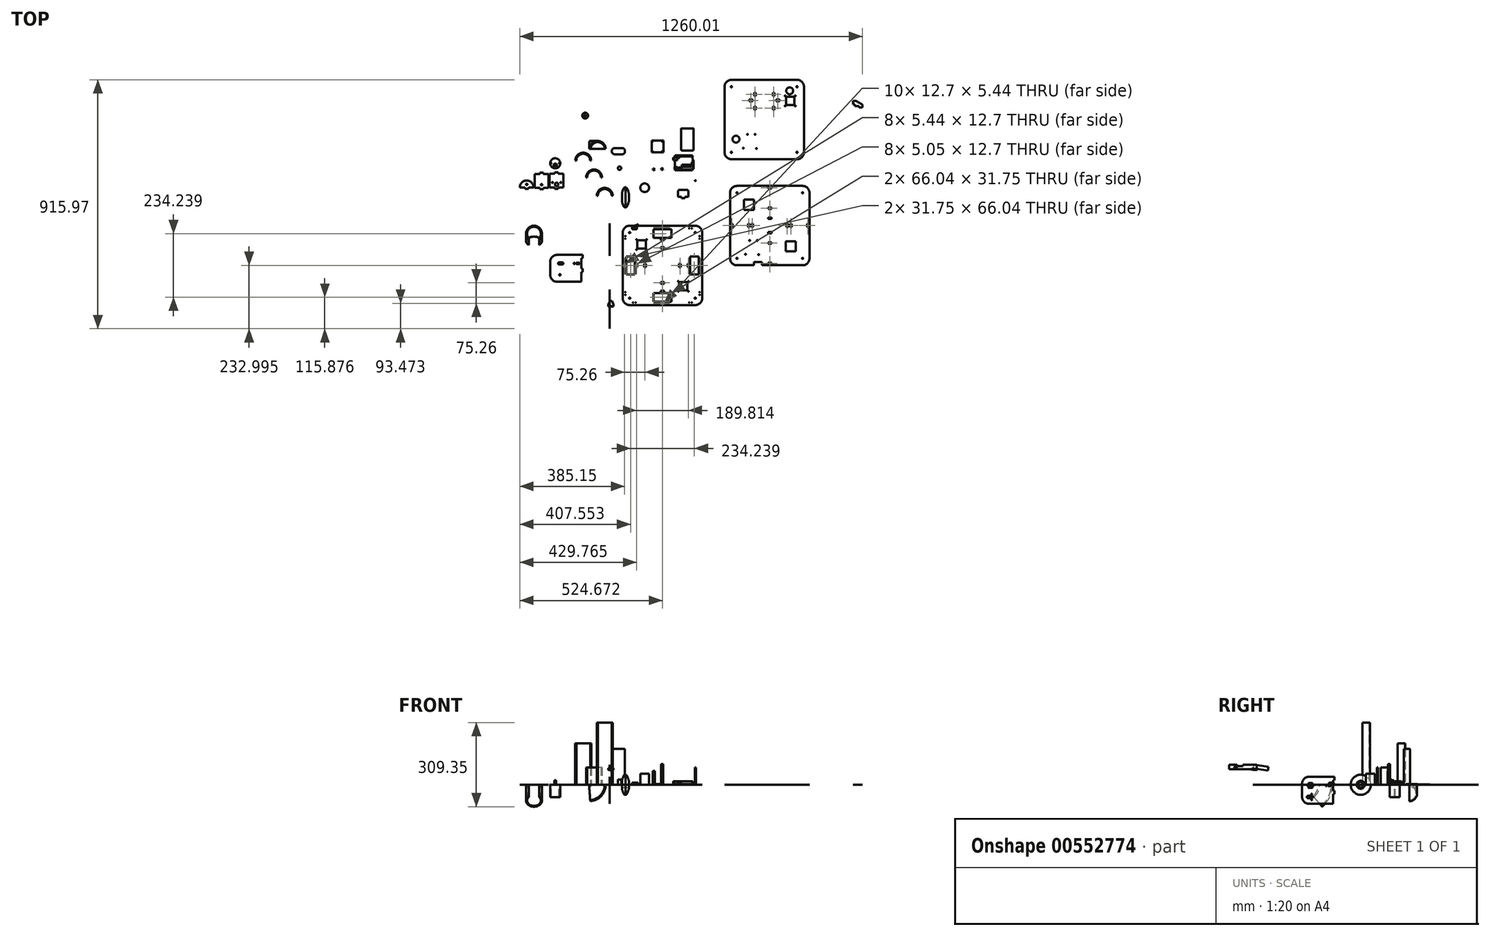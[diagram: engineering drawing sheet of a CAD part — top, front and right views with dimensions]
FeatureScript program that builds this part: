
annotation { "Feature Type Name" : "Feature", "Feature Type Description" : "" }
export const myFeature = defineFeature(function(context is Context, id is Id, definition is map)
    precondition{}
    {
        {
            assignVariable(context, id + "F0", {"name" : "T0", "anyValue" : .214});
        }
        {
            var Q0;
            Q0=qCreatedBy(makeId("Top.planeOp"),FACE);
            var sketch = newSketch(context, id + "F1", { "sketchPlane" : qUnion([Q0])});
            skCircle(sketch, "E0", {"center": v(-195, -13.55) * mm, "radius": 6.25 * mm});
            skCircle(sketch, "E1", {"center": v(-210.5, -6.55) * mm, "radius": 1.7 * mm});
            skCircle(sketch, "E2", {"center": v(-250.53, -14.94) * mm, "radius": 2.48 * mm});
            skLineSegment(sketch, "E3", {"start": v(-250.53, 35.96) * mm, "end": v(-250.53, -27.42) * mm, "construction": true});
            skLineSegment(sketch, "E4", {"start": v(-195, -13.55) * mm, "end": v(-195, 25.75) * mm, "construction": true});
            skLineSegment(sketch, "E5.bottom", {"start": v(-220.4, -25.05) * mm, "end": v(-201.34, -25.05) * mm});
            skLineSegment(sketch, "E5.top", {"start": v(-220.4, 25.75) * mm, "end": v(-201.34, 25.75) * mm});
            skLineSegment(sketch, "E5.left", {"start": v(-220.4, -25.05) * mm, "end": v(-220.4, 25.75) * mm});
            skLineSegment(sketch, "E5.right", {"start": v(-169.6, -25.05) * mm, "end": v(-169.6, 25.75) * mm});
            skLineSegment(sketch, "E6.top", {"start": v(-188.64, -30.48) * mm, "end": v(-201.34, -30.48) * mm});
            skLineSegment(sketch, "E6.left", {"start": v(-188.64, -25.05) * mm, "end": v(-188.64, -30.48) * mm});
            skLineSegment(sketch, "E6.right", {"start": v(-201.34, -25.05) * mm, "end": v(-201.34, -30.48) * mm});
            skPoint(sketch, "E6.middle", {"position": v(-195, -27.76) * mm});
            skCircle(sketch, "E7.MirrorC", {"center": v(-179.5, -6.55) * mm, "radius": 1.7 * mm});
            skLineSegment(sketch, "E8.trimOffspring", {"start": v(-188.64, -25.05) * mm, "end": v(-169.6, -25.05) * mm});
            skLineSegment(sketch, "E9.top", {"start": v(-188.64, 31.2) * mm, "end": v(-201.34, 31.2) * mm});
            skLineSegment(sketch, "E9.left", {"start": v(-188.64, 25.75) * mm, "end": v(-188.64, 31.2) * mm});
            skLineSegment(sketch, "E9.right", {"start": v(-201.34, 25.75) * mm, "end": v(-201.34, 31.2) * mm});
            skPoint(sketch, "E9.middle", {"position": v(-195, 28.47) * mm});
            skLineSegment(sketch, "E10.trimOffspring", {"start": v(-188.64, 25.75) * mm, "end": v(-169.6, 25.75) * mm});
            skLineSegment(sketch, "E11.bottom", {"start": v(-225.13, 24.36) * mm, "end": v(-244.18, 24.36) * mm});
            skLineSegment(sketch, "E11.top", {"start": v(-225.13, -26.44) * mm, "end": v(-244.18, -26.44) * mm});
            skLineSegment(sketch, "E11.left", {"start": v(-225.13, 24.36) * mm, "end": v(-225.13, -26.44) * mm});
            skLineSegment(sketch, "E11.right", {"start": v(-275.93, 24.36) * mm, "end": v(-275.93, -26.44) * mm});
            skPoint(sketch, "E11.middle", {"position": v(-250.53, -1.04) * mm});
            skLineSegment(sketch, "E12.top", {"start": v(-244.18, 29.8) * mm, "end": v(-256.88, 29.8) * mm});
            skLineSegment(sketch, "E12.left", {"start": v(-244.18, 24.36) * mm, "end": v(-244.18, 29.8) * mm});
            skLineSegment(sketch, "E12.right", {"start": v(-256.88, 24.36) * mm, "end": v(-256.88, 29.8) * mm});
            skPoint(sketch, "E12.middle", {"position": v(-250.53, 27.08) * mm});
            skLineSegment(sketch, "E13.trimOffspring", {"start": v(-256.88, 24.36) * mm, "end": v(-275.93, 24.36) * mm});
            skLineSegment(sketch, "E14.top", {"start": v(-244.18, -31.88) * mm, "end": v(-256.88, -31.88) * mm});
            skLineSegment(sketch, "E14.left", {"start": v(-244.18, -26.44) * mm, "end": v(-244.18, -31.88) * mm});
            skLineSegment(sketch, "E14.right", {"start": v(-256.88, -26.44) * mm, "end": v(-256.88, -31.88) * mm});
            skPoint(sketch, "E14.middle", {"position": v(-250.53, -29.16) * mm});
            skLineSegment(sketch, "E15.trimOffspring", {"start": v(-256.88, -26.44) * mm, "end": v(-275.93, -26.44) * mm});
            skCircle(sketch, "E16", {"center": v(-304.98, -13.55) * mm, "radius": 2.48 * mm});
            skLineSegment(sketch, "E17", {"start": v(-310.06, 36.93) * mm, "end": v(-310.06, -26.44) * mm, "construction": true});
            skLineSegment(sketch, "E18.top", {"start": v(-279.58, -25.05) * mm, "end": v(-298.63, -25.05) * mm});
            skPoint(sketch, "E18.middle", {"position": v(-304.98, 0.35) * mm});
            skLineSegment(sketch, "E19.top", {"start": v(-298.63, -30.48) * mm, "end": v(-311.33, -30.48) * mm});
            skLineSegment(sketch, "E19.left", {"start": v(-298.63, -25.05) * mm, "end": v(-298.63, -30.48) * mm});
            skLineSegment(sketch, "E19.right", {"start": v(-311.33, -25.05) * mm, "end": v(-311.33, -30.48) * mm});
            skPoint(sketch, "E19.middle", {"position": v(-304.98, -27.76) * mm});
            skLineSegment(sketch, "E20.trimOffspring", {"start": v(-311.33, -25.05) * mm, "end": v(-330.38, -25.05) * mm});
            skArc(sketch, "E21", {"start": v(-279.58, -25.05) * mm, "mid": v(-304.98, 0.35) * mm, "end": v(-330.38, -25.05) * mm});
            skSolve(sketch);
        }
        {
            var Q0;
            Q0=qCreatedBy(makeId("Top.planeOp"),FACE);
            var sketch = newSketch(context, id + "F2", { "sketchPlane" : qUnion([Q0])});
            skCircle(sketch, "E22", {"center": v(-200.16, 64.01) * mm, "radius": 18.5 * mm});
            skLineSegment(sketch, "E23", {"start": v(-200.16, 64.01) * mm, "end": v(-200.16, 82.51) * mm, "construction": true});
            skLineSegment(sketch, "E24", {"start": v(-200.16, 64.01) * mm, "end": v(-218.66, 64.01) * mm, "construction": true});
            skCircle(sketch, "E25", {"center": v(-215.66, 64.01) * mm, "radius": 1.7 * mm});
            skLineSegment(sketch, "E26", {"start": v(-200.16, 64.01) * mm, "end": v(-200.16, 45.51) * mm, "construction": true});
            skCircle(sketch, "E27", {"center": v(-200.16, 57.01) * mm, "radius": 3 * mm});
            skCircle(sketch, "E28.MirrorC", {"center": v(-184.66, 64.01) * mm, "radius": 1.7 * mm});
            skCircle(sketch, "E29", {"center": v(-200.16, 57.01) * mm, "radius": 6 * mm});
            skSolve(sketch);
        }
        {
            var Q0;
            Q0=makeQuery(id+"F2.imprint","IMPRINT",FACE,{"disambiguationData":[TD([[makeQuery(id+"F2.imprint","IMPRINT",EDGE,{"derivedFrom":sQuery(id+"F2.wireOp",EDGE,"VeMokPUN-uezl-VlB1-s7x8-Obfx0nJFnMSX")}),1.0]])]});
            var Q1;
            Q1=makeQuery(id+"F2.imprint","IMPRINT",FACE,{"disambiguationData":[TD([[makeQuery(id+"F2.imprint","IMPRINT",EDGE,{"derivedFrom":sQuery(id+"F2.wireOp",EDGE,"E22")}),1.0]])]});
            var Q2;
            Q2=makeQuery(id+"F2.imprint","IMPRINT",FACE,{"disambiguationData":[TD([[makeQuery(id+"F2.imprint","IMPRINT",EDGE,{"derivedFrom":sQuery(id+"F2.wireOp",EDGE,"E27")}),1.0]])]});
            var Q3;
            Q3=makeQuery(id+"F2.imprint","IMPRINT",FACE,{"disambiguationData":[TD([[makeQuery(id+"F2.imprint","IMPRINT",EDGE,{"derivedFrom":sQuery(id+"F2.wireOp",EDGE,"E27")}),-1.0]])]});
            extrude(context, id + "F3", {"entities" : qUnion([Q0, Q1, Q2, Q3]), "oppositeDirection" : true, "depth" : 45.4 * mm, "offsetDistance" : 25.4 * mm});
        }
        {
            var Q0;
            Q0=makeQuery(id+"F3.opExtrude","CAP_FACE",FACE,{"disambiguationData":[OSD([sQuery(id+"F2.wireOp",EDGE,"E22"),sQuery(id+"F2.wireOp",EDGE,"E25"),sQuery(id+"F2.wireOp",EDGE,"E28.MirrorC")])],"isStart":true});
            var sketch = newSketch(context, id + "F4", { "sketchPlane" : qUnion([Q0])});
            skLineSegment(sketch, "E30", {"start": v(-215.66, 64.01) * mm, "end": v(-184.66, 64.01) * mm, "construction": true});
            skLineSegment(sketch, "E31", {"start": v(-200.16, 64.01) * mm, "end": v(-200.16, 45.51) * mm, "construction": true});
            skCircle(sketch, "E32", {"center": v(-200.16, 57.01) * mm, "radius": 6 * mm});
            skSolve(sketch);
        }
        {
            var Q0;
            Q0=makeQuery(id+"F4.imprint","IMPRINT",FACE,{"disambiguationData":[TD([[makeQuery(id+"F4.imprint","IMPRINT",EDGE,{"derivedFrom":sQuery(id+"F4.wireOp",EDGE,"E32")}),1.0]])]});
            extrude(context, id + "F5", {"entities" : qUnion([Q0]), "operationType" : NewBodyOperationType.ADD, "depth" : 4 * mm, "offsetDistance" : 25.4 * mm});
        }
        {
            var Q0;
            Q0=makeQuery(id+"F5.opExtrude","CAP_FACE",FACE,{"disambiguationData":[OSD([sQuery(id+"F4.wireOp",EDGE,"E32")])],"isStart":false});
            var sketch = newSketch(context, id + "F6", { "sketchPlane" : qUnion([Q0])});
            skCircle(sketch, "E33", {"center": v(-200.16, 57.01) * mm, "radius": 3 * mm});
            skSolve(sketch);
        }
        {
            var Q0;
            Q0=makeQuery(id+"F6.imprint","IMPRINT",FACE,{"disambiguationData":[TD([[makeQuery(id+"F6.imprint","IMPRINT",EDGE,{"derivedFrom":sQuery(id+"F6.wireOp",EDGE,"E33")}),1.0]])]});
            extrude(context, id + "F7", {"entities" : qUnion([Q0]), "operationType" : NewBodyOperationType.ADD, "depth" : 13 * mm, "offsetDistance" : 25.4 * mm});
        }
        {
            var Q0;
            Q0=qCreatedBy(makeId("Top.planeOp"),FACE);
            var sketch = newSketch(context, id + "F8", { "sketchPlane" : qUnion([Q0])});
            skLineSegment(sketch, "E34.bottom", {"start": v(154.77, 147.35) * mm, "end": v(197.77, 147.35) * mm});
            skLineSegment(sketch, "E34.top", {"start": v(154.77, 104.35) * mm, "end": v(197.77, 104.35) * mm});
            skLineSegment(sketch, "E34.left", {"start": v(154.77, 147.35) * mm, "end": v(154.77, 104.35) * mm});
            skLineSegment(sketch, "E34.right", {"start": v(197.77, 147.35) * mm, "end": v(197.77, 104.35) * mm});
            skCircle(sketch, "E35", {"center": v(157.22, 144.54) * mm, "radius": 1.74 * mm});
            skCircle(sketch, "E36.0.1.0", {"center": v(157.22, 107.54) * mm, "radius": 1.74 * mm});
            skCircle(sketch, "E36.1.0.0", {"center": v(194.22, 144.54) * mm, "radius": 1.74 * mm});
            skCircle(sketch, "E36.1.1.0", {"center": v(194.22, 107.54) * mm, "radius": 1.74 * mm});
            skLineSegment(sketch, "E36.direction1", {"start": v(157.22, 144.54) * mm, "end": v(194.22, 144.54) * mm, "construction": true});
            skLineSegment(sketch, "E36.direction2", {"start": v(157.22, 144.54) * mm, "end": v(157.22, 107.54) * mm, "construction": true});
            skSolve(sketch);
        }
        {
            var Q0;
            Q0 = qSketchRegion(id + "F8", true);
            extrude(context, id + "F9", {"entities" : qUnion([Q0]), "depth" : 2.03 * mm, "offsetDistance" : 25.4 * mm});
        }
        {
            var Q0;
            Q0=qCreatedBy(makeId("Top.planeOp"),FACE);
            var sketch = newSketch(context, id + "F10", { "sketchPlane" : qUnion([Q0])});
            skLineSegment(sketch, "E37.bottom", {"start": v(18.32, 97.14) * mm, "end": v(46.26, 97.14) * mm});
            skLineSegment(sketch, "E37.top", {"start": v(18.32, 120) * mm, "end": v(46.26, 120) * mm});
            skLineSegment(sketch, "E37.left", {"start": v(8.16, 107.3) * mm, "end": v(8.16, 109.84) * mm});
            skLineSegment(sketch, "E37.right", {"start": v(56.42, 107.3) * mm, "end": v(56.42, 109.84) * mm});
            skPoint(sketch, "E38.visualSharp", {"position": v(8.16, 120) * mm});
            skArc(sketch, "E38.filletArc", {"start": v(18.32, 120) * mm, "mid": v(11.13, 117.02) * mm, "end": v(8.16, 109.84) * mm});
            skPoint(sketch, "E39.visualSharp", {"position": v(8.16, 97.14) * mm});
            skArc(sketch, "E39.filletArc", {"start": v(8.16, 107.3) * mm, "mid": v(11.13, 100.12) * mm, "end": v(18.32, 97.14) * mm});
            skPoint(sketch, "E40.visualSharp", {"position": v(56.42, 97.14) * mm});
            skArc(sketch, "E40.filletArc", {"start": v(46.26, 97.14) * mm, "mid": v(53.44, 100.12) * mm, "end": v(56.42, 107.3) * mm});
            skPoint(sketch, "E41.visualSharp", {"position": v(56.42, 120) * mm});
            skArc(sketch, "E41.filletArc", {"start": v(56.42, 109.84) * mm, "mid": v(53.44, 117.02) * mm, "end": v(46.26, 120) * mm});
            skSolve(sketch);
        }
        {
            var Q0;
            Q0 = qSketchRegion(id + "F10", true);
            extrude(context, id + "F11", {"entities" : qUnion([Q0]), "depth" : 132.08 * mm, "offsetDistance" : 25.4 * mm});
        }
        {
            var Q0;
            Q0=qCreatedBy(makeId("Top.planeOp"),FACE);
            var sketch = newSketch(context, id + "F12", { "sketchPlane" : qUnion([Q0])});
            skLineSegment(sketch, "E42.bottom", {"start": v(240.3, 92.55) * mm, "end": v(305.07, 92.55) * mm});
            skLineSegment(sketch, "E42.top", {"start": v(240.3, 38.58) * mm, "end": v(305.07, 38.58) * mm});
            skLineSegment(sketch, "E42.left", {"start": v(240.3, 92.55) * mm, "end": v(240.3, 38.58) * mm});
            skLineSegment(sketch, "E42.right", {"start": v(305.07, 92.55) * mm, "end": v(305.07, 78.55) * mm});
            skLineSegment(sketch, "E43", {"start": v(305.07, 78.55) * mm, "end": v(308.97, 75.22) * mm});
            skLineSegment(sketch, "E44", {"start": v(308.97, 75.22) * mm, "end": v(308.97, 43.61) * mm});
            skLineSegment(sketch, "E45", {"start": v(308.97, 43.61) * mm, "end": v(305.07, 40.9) * mm});
            skLineSegment(sketch, "E46.trimOffspring", {"start": v(305.07, 40.9) * mm, "end": v(305.07, 38.58) * mm});
            skCircle(sketch, "E47", {"center": v(254.27, 41.12) * mm, "radius": 1.59 * mm});
            skCircle(sketch, "E48", {"center": v(306.34, 46.2) * mm, "radius": 1.59 * mm});
            skCircle(sketch, "E49", {"center": v(306.34, 74.14) * mm, "radius": 1.59 * mm});
            skCircle(sketch, "E50", {"center": v(255.54, 89.38) * mm, "radius": 1.59 * mm});
            skSolve(sketch);
        }
        {
            var Q0;
            Q0 = qSketchRegion(id + "F12", true);
            extrude(context, id + "F13", {"entities" : qUnion([Q0]), "depth" : 3.17 * mm, "offsetDistance" : 25.4 * mm});
        }
        {
            var Q0;
            Q0=makeQuery(id+"F13.opExtrude","CAP_FACE",FACE,{"disambiguationData":[OSD([sQuery(id+"F12.wireOp",EDGE,"E42.bottom"),sQuery(id+"F12.wireOp",EDGE,"E42.top"),sQuery(id+"F12.wireOp",EDGE,"E42.left"),sQuery(id+"F12.wireOp",EDGE,"E42.right"),sQuery(id+"F12.wireOp",EDGE,"E43"),sQuery(id+"F12.wireOp",EDGE,"E44"),sQuery(id+"F12.wireOp",EDGE,"E45"),sQuery(id+"F12.wireOp",EDGE,"E46.trimOffspring")])],"isStart":false});
            var sketch = newSketch(context, id + "F14", { "sketchPlane" : qUnion([Q0])});
            skLineSegment(sketch, "E51.bottom", {"start": v(253.63, 91.4) * mm, "end": v(305.07, 91.4) * mm});
            skLineSegment(sketch, "E51.top", {"start": v(253.63, 89.59) * mm, "end": v(305.07, 89.59) * mm});
            skLineSegment(sketch, "E51.left", {"start": v(253.63, 91.4) * mm, "end": v(253.63, 89.59) * mm});
            skLineSegment(sketch, "E51.right", {"start": v(305.07, 91.4) * mm, "end": v(305.07, 89.59) * mm});
            skLineSegment(sketch, "E52.bottom", {"start": v(260.74, 39.85) * mm, "end": v(303.83, 39.85) * mm});
            skLineSegment(sketch, "E52.top", {"start": v(260.74, 41.36) * mm, "end": v(303.83, 41.36) * mm});
            skLineSegment(sketch, "E52.left", {"start": v(260.74, 39.85) * mm, "end": v(260.74, 41.36) * mm});
            skLineSegment(sketch, "E52.right", {"start": v(303.83, 39.85) * mm, "end": v(303.83, 41.36) * mm});
            skLineSegment(sketch, "E53.bottom", {"start": v(264.97, 58.14) * mm, "end": v(300.65, 58.14) * mm});
            skLineSegment(sketch, "E53.top", {"start": v(264.97, 51.03) * mm, "end": v(300.65, 51.03) * mm});
            skLineSegment(sketch, "E53.left", {"start": v(264.97, 58.14) * mm, "end": v(264.97, 51.03) * mm});
            skLineSegment(sketch, "E53.right", {"start": v(300.65, 58.14) * mm, "end": v(300.65, 51.03) * mm});
            skCircle(sketch, "E54", {"center": v(255.9, 46.65) * mm, "radius": 2.27 * mm});
            skCircle(sketch, "E55", {"center": v(261.2, 46.65) * mm, "radius": 2.46 * mm});
            skLineSegment(sketch, "E56.bottom", {"start": v(238.52, 49.52) * mm, "end": v(250.61, 49.52) * mm});
            skLineSegment(sketch, "E56.top", {"start": v(238.52, 43.17) * mm, "end": v(250.61, 43.17) * mm});
            skLineSegment(sketch, "E56.left", {"start": v(238.52, 49.52) * mm, "end": v(238.52, 43.17) * mm});
            skLineSegment(sketch, "E56.right", {"start": v(250.61, 49.52) * mm, "end": v(250.61, 43.17) * mm});
            skLineSegment(sketch, "E57.bottom", {"start": v(233.38, 85.35) * mm, "end": v(248.34, 85.35) * mm});
            skLineSegment(sketch, "E57.top", {"start": v(233.38, 75.22) * mm, "end": v(248.34, 75.22) * mm});
            skLineSegment(sketch, "E57.left", {"start": v(233.38, 85.35) * mm, "end": v(233.38, 75.22) * mm});
            skLineSegment(sketch, "E57.right", {"start": v(248.34, 85.35) * mm, "end": v(248.34, 75.22) * mm});
            skLineSegment(sketch, "E58.bottom", {"start": v(302.77, 68.72) * mm, "end": v(305.8, 68.72) * mm});
            skLineSegment(sketch, "E58.top", {"start": v(302.77, 63.28) * mm, "end": v(305.8, 63.28) * mm});
            skLineSegment(sketch, "E58.left", {"start": v(302.77, 68.72) * mm, "end": v(302.77, 63.28) * mm});
            skLineSegment(sketch, "E58.right", {"start": v(305.8, 68.72) * mm, "end": v(305.8, 63.28) * mm});
            skLineSegment(sketch, "E59.bottom", {"start": v(250.91, 87.62) * mm, "end": v(257.41, 87.62) * mm});
            skLineSegment(sketch, "E59.top", {"start": v(250.91, 84.45) * mm, "end": v(257.41, 84.45) * mm});
            skLineSegment(sketch, "E59.left", {"start": v(250.91, 87.62) * mm, "end": v(250.91, 84.45) * mm});
            skLineSegment(sketch, "E59.right", {"start": v(257.41, 87.62) * mm, "end": v(257.41, 84.45) * mm});
            skSolve(sketch);
        }
        {
            var Q0;
            Q0 = qSketchRegion(id + "F14", true);
            extrude(context, id + "F15", {"entities" : qUnion([Q0]), "operationType" : NewBodyOperationType.ADD, "depth" : 9.52 * mm, "offsetDistance" : 25.4 * mm});
        }
        {
            var Q0;
            Q0 = qSketchRegion(id + "F1", true);
            extrude(context, id + "F16", {"entities" : qUnion([Q0]), "depth" : (getVariable(context, 'T0')) * mm, "offsetDistance" : 25.4 * mm});
        }
        {
            var Q0;
            Q0=qCreatedBy(makeId("Top.planeOp"),FACE);
            var sketch = newSketch(context, id + "F17", { "sketchPlane" : qUnion([Q0])});
            skLineSegment(sketch, "E60.bottom", {"start": v(314.94, -165.87) * mm, "end": v(73.64, -165.87) * mm});
            skLineSegment(sketch, "E60.top", {"start": v(314.94, -457.97) * mm, "end": v(73.64, -457.97) * mm});
            skLineSegment(sketch, "E60.left", {"start": v(340.34, -191.27) * mm, "end": v(340.34, -432.57) * mm});
            skLineSegment(sketch, "E60.right", {"start": v(48.24, -191.27) * mm, "end": v(48.24, -432.57) * mm});
            skPoint(sketch, "E60.middle", {"position": v(194.3, -311.92) * mm});
            skPoint(sketch, "E61.visualSharp", {"position": v(48.24, -165.87) * mm});
            skArc(sketch, "E61.filletArc", {"start": v(73.64, -165.87) * mm, "mid": v(55.68, -173.31) * mm, "end": v(48.24, -191.27) * mm});
            skPoint(sketch, "E62.visualSharp", {"position": v(340.34, -165.87) * mm});
            skArc(sketch, "E62.filletArc", {"start": v(340.34, -191.27) * mm, "mid": v(332.9, -173.31) * mm, "end": v(314.94, -165.87) * mm});
            skPoint(sketch, "E63.visualSharp", {"position": v(340.34, -457.97) * mm});
            skArc(sketch, "E63.filletArc", {"start": v(314.94, -457.97) * mm, "mid": v(332.9, -450.54) * mm, "end": v(340.34, -432.57) * mm});
            skPoint(sketch, "E64.visualSharp", {"position": v(48.24, -457.97) * mm});
            skArc(sketch, "E64.filletArc", {"start": v(48.24, -432.57) * mm, "mid": v(55.68, -450.54) * mm, "end": v(73.64, -457.97) * mm});
            skLineSegment(sketch, "E65", {"start": v(194.3, -165.87) * mm, "end": v(194.3, -311.92) * mm, "construction": true});
            skLineSegment(sketch, "E66.bottom", {"start": v(200.64, -169.68) * mm, "end": v(187.94, -169.68) * mm});
            skLineSegment(sketch, "E66.top", {"start": v(200.64, -175.12) * mm, "end": v(187.94, -175.12) * mm});
            skLineSegment(sketch, "E66.left", {"start": v(200.64, -169.68) * mm, "end": v(200.64, -175.12) * mm});
            skLineSegment(sketch, "E66.right", {"start": v(187.94, -169.68) * mm, "end": v(187.94, -175.12) * mm});
            skPoint(sketch, "E66.middle", {"position": v(194.3, -172.4) * mm});
            skLineSegment(sketch, "E67.bottom", {"start": v(227.31, -178.93) * mm, "end": v(161.27, -178.93) * mm});
            skLineSegment(sketch, "E67.top", {"start": v(227.31, -210.68) * mm, "end": v(161.27, -210.68) * mm});
            skLineSegment(sketch, "E67.left", {"start": v(227.31, -178.93) * mm, "end": v(227.31, -210.68) * mm});
            skLineSegment(sketch, "E67.right", {"start": v(161.27, -178.93) * mm, "end": v(161.27, -210.68) * mm});
            skPoint(sketch, "E67.middle", {"position": v(194.3, -194.8) * mm});
            skPoint(sketch, "E68.middle", {"position": v(194.3, -217.02) * mm});
            skLineSegment(sketch, "E69.bottom", {"start": v(200.64, -214.5) * mm, "end": v(187.94, -214.5) * mm});
            skLineSegment(sketch, "E69.top", {"start": v(200.64, -219.55) * mm, "end": v(187.94, -219.55) * mm});
            skLineSegment(sketch, "E69.left", {"start": v(200.64, -214.5) * mm, "end": v(200.64, -219.55) * mm});
            skLineSegment(sketch, "E69.right", {"start": v(187.94, -214.5) * mm, "end": v(187.94, -219.55) * mm});
            skLineSegment(sketch, "E70.bottom", {"start": v(200.64, -244.95) * mm, "end": v(187.94, -244.95) * mm});
            skLineSegment(sketch, "E70.top", {"start": v(200.64, -250.38) * mm, "end": v(187.94, -250.38) * mm});
            skLineSegment(sketch, "E70.left", {"start": v(200.64, -244.95) * mm, "end": v(200.64, -250.38) * mm});
            skLineSegment(sketch, "E70.right", {"start": v(187.94, -244.95) * mm, "end": v(187.94, -250.38) * mm});
            skPoint(sketch, "E70.middle", {"position": v(194.3, -247.66) * mm});
            skCircle(sketch, "E71", {"center": v(73.64, -191.27) * mm, "radius": 2.13 * mm});
            skCircle(sketch, "E72.1.0", {"center": v(314.94, -191.27) * mm, "radius": 2.13 * mm});
            skLineSegment(sketch, "E72.1.1", {"start": v(327.29, -278.9) * mm, "end": v(295.54, -278.9) * mm});
            skLineSegment(sketch, "E72.1.2", {"start": v(327.29, -344.94) * mm, "end": v(327.29, -278.9) * mm});
            skLineSegment(sketch, "E72.1.3", {"start": v(295.54, -344.94) * mm, "end": v(295.54, -278.9) * mm});
            skLineSegment(sketch, "E72.1.4", {"start": v(327.29, -344.94) * mm, "end": v(295.54, -344.94) * mm});
            skLineSegment(sketch, "E72.1.5", {"start": v(331.1, -318.27) * mm, "end": v(331.1, -305.57) * mm});
            skLineSegment(sketch, "E72.1.6", {"start": v(336.53, -305.57) * mm, "end": v(331.1, -305.57) * mm});
            skLineSegment(sketch, "E72.1.7", {"start": v(336.53, -318.27) * mm, "end": v(336.53, -305.57) * mm});
            skLineSegment(sketch, "E72.1.8", {"start": v(336.53, -318.27) * mm, "end": v(331.1, -318.27) * mm});
            skLineSegment(sketch, "E72.1.9", {"start": v(291.73, -318.27) * mm, "end": v(291.73, -305.57) * mm});
            skLineSegment(sketch, "E72.1.10", {"start": v(291.73, -305.57) * mm, "end": v(286.67, -305.57) * mm});
            skLineSegment(sketch, "E72.1.11", {"start": v(286.67, -318.27) * mm, "end": v(286.67, -305.57) * mm});
            skLineSegment(sketch, "E72.1.12", {"start": v(291.73, -318.27) * mm, "end": v(286.67, -318.27) * mm});
            skLineSegment(sketch, "E72.1.13", {"start": v(261.27, -318.27) * mm, "end": v(261.27, -305.57) * mm});
            skLineSegment(sketch, "E72.1.14", {"start": v(261.27, -318.27) * mm, "end": v(255.84, -318.27) * mm});
            skLineSegment(sketch, "E72.1.15", {"start": v(255.84, -318.27) * mm, "end": v(255.84, -305.57) * mm});
            skLineSegment(sketch, "E72.1.16", {"start": v(261.27, -305.57) * mm, "end": v(255.84, -305.57) * mm});
            skCircle(sketch, "E72.2.0", {"center": v(314.94, -432.57) * mm, "radius": 2.13 * mm});
            skLineSegment(sketch, "E72.2.1", {"start": v(227.31, -444.92) * mm, "end": v(227.31, -413.17) * mm});
            skLineSegment(sketch, "E72.2.2", {"start": v(161.27, -444.92) * mm, "end": v(227.31, -444.92) * mm});
            skLineSegment(sketch, "E72.2.3", {"start": v(161.27, -413.17) * mm, "end": v(227.31, -413.17) * mm});
            skLineSegment(sketch, "E72.2.4", {"start": v(161.27, -444.92) * mm, "end": v(161.27, -413.17) * mm});
            skLineSegment(sketch, "E72.2.5", {"start": v(187.94, -448.73) * mm, "end": v(200.64, -448.73) * mm});
            skLineSegment(sketch, "E72.2.6", {"start": v(200.64, -454.16) * mm, "end": v(200.64, -448.73) * mm});
            skLineSegment(sketch, "E72.2.7", {"start": v(187.94, -454.16) * mm, "end": v(200.64, -454.16) * mm});
            skLineSegment(sketch, "E72.2.8", {"start": v(187.94, -454.16) * mm, "end": v(187.94, -448.73) * mm});
            skLineSegment(sketch, "E72.2.9", {"start": v(187.94, -409.36) * mm, "end": v(200.64, -409.36) * mm});
            skLineSegment(sketch, "E72.2.10", {"start": v(200.64, -409.36) * mm, "end": v(200.64, -404.3) * mm});
            skLineSegment(sketch, "E72.2.11", {"start": v(187.94, -404.3) * mm, "end": v(200.64, -404.3) * mm});
            skLineSegment(sketch, "E72.2.12", {"start": v(187.94, -409.36) * mm, "end": v(187.94, -404.3) * mm});
            skLineSegment(sketch, "E72.2.13", {"start": v(187.94, -378.9) * mm, "end": v(200.64, -378.9) * mm});
            skLineSegment(sketch, "E72.2.14", {"start": v(187.94, -378.9) * mm, "end": v(187.94, -373.47) * mm});
            skLineSegment(sketch, "E72.2.15", {"start": v(187.94, -373.47) * mm, "end": v(200.64, -373.47) * mm});
            skLineSegment(sketch, "E72.2.16", {"start": v(200.64, -378.9) * mm, "end": v(200.64, -373.47) * mm});
            skCircle(sketch, "E72.3.0", {"center": v(73.64, -432.57) * mm, "radius": 2.13 * mm});
            skLineSegment(sketch, "E72.3.1", {"start": v(61.3, -344.94) * mm, "end": v(93.05, -344.94) * mm});
            skLineSegment(sketch, "E72.3.2", {"start": v(61.3, -278.9) * mm, "end": v(61.3, -344.94) * mm});
            skLineSegment(sketch, "E72.3.3", {"start": v(93.05, -278.9) * mm, "end": v(93.05, -344.94) * mm});
            skLineSegment(sketch, "E72.3.4", {"start": v(61.3, -278.9) * mm, "end": v(93.05, -278.9) * mm});
            skLineSegment(sketch, "E72.3.5", {"start": v(57.49, -305.57) * mm, "end": v(57.49, -318.27) * mm});
            skLineSegment(sketch, "E72.3.6", {"start": v(52.05, -318.27) * mm, "end": v(57.49, -318.27) * mm});
            skLineSegment(sketch, "E72.3.7", {"start": v(52.05, -305.57) * mm, "end": v(52.05, -318.27) * mm});
            skLineSegment(sketch, "E72.3.8", {"start": v(52.05, -305.57) * mm, "end": v(57.49, -305.57) * mm});
            skLineSegment(sketch, "E72.3.9", {"start": v(96.86, -305.57) * mm, "end": v(96.86, -318.27) * mm});
            skLineSegment(sketch, "E72.3.10", {"start": v(96.86, -318.27) * mm, "end": v(101.91, -318.27) * mm});
            skLineSegment(sketch, "E72.3.11", {"start": v(101.91, -305.57) * mm, "end": v(101.91, -318.27) * mm});
            skLineSegment(sketch, "E72.3.12", {"start": v(96.86, -305.57) * mm, "end": v(101.91, -305.57) * mm});
            skLineSegment(sketch, "E72.3.13", {"start": v(127.31, -305.57) * mm, "end": v(127.31, -318.27) * mm});
            skLineSegment(sketch, "E72.3.14", {"start": v(127.31, -305.57) * mm, "end": v(132.75, -305.57) * mm});
            skLineSegment(sketch, "E72.3.15", {"start": v(132.75, -305.57) * mm, "end": v(132.75, -318.27) * mm});
            skLineSegment(sketch, "E72.3.16", {"start": v(127.31, -318.27) * mm, "end": v(132.75, -318.27) * mm});
            skLineSegment(sketch, "E72.anchor1", {"start": v(194.3, -311.92) * mm, "end": v(73.64, -191.27) * mm, "construction": true});
            skLineSegment(sketch, "E72.anchor2", {"start": v(194.3, -311.92) * mm, "end": v(73.64, -432.57) * mm, "construction": true});
            skCircle(sketch, "E73", {"center": v(99.04, -216.67) * mm, "radius": 1.46 * mm});
            skCircle(sketch, "E74.0.1.0", {"center": v(99.04, -253.67) * mm, "radius": 1.46 * mm});
            skCircle(sketch, "E74.1.0.0", {"center": v(136.04, -216.67) * mm, "radius": 1.46 * mm});
            skCircle(sketch, "E74.1.1.0", {"center": v(136.04, -253.67) * mm, "radius": 1.46 * mm});
            skLineSegment(sketch, "E74.direction1", {"start": v(94.2, -207.7) * mm, "end": v(130.01, -207.7) * mm, "construction": true});
            skLineSegment(sketch, "E74.direction2", {"start": v(94.2, -207.7) * mm, "end": v(94.2, -243.5) * mm, "construction": true});
            skCircle(sketch, "E75.1.0", {"center": v(252.54, -407.17) * mm, "radius": 1.46 * mm});
            skCircle(sketch, "E75.1.1", {"center": v(289.54, -407.17) * mm, "radius": 1.46 * mm});
            skCircle(sketch, "E75.1.2", {"center": v(289.54, -370.17) * mm, "radius": 1.46 * mm});
            skCircle(sketch, "E75.1.3", {"center": v(252.54, -370.17) * mm, "radius": 1.46 * mm});
            skLineSegment(sketch, "E75.anchor1", {"start": v(194.3, -311.92) * mm, "end": v(136.04, -216.67) * mm, "construction": true});
            skLineSegment(sketch, "E75.anchor2", {"start": v(194.3, -311.92) * mm, "end": v(252.54, -407.17) * mm, "construction": true});
            skCircle(sketch, "E76", {"center": v(86.34, -175.4) * mm, "radius": 1.02 * mm});
            skCircle(sketch, "E77", {"center": v(95.87, -175.4) * mm, "radius": 1.02 * mm});
            skCircle(sketch, "E78.MirrorC", {"center": v(302.24, -175.4) * mm, "radius": 1.02 * mm});
            skCircle(sketch, "E79.MirrorC", {"center": v(292.72, -175.4) * mm, "radius": 1.02 * mm});
            skCircle(sketch, "E80.1.0", {"center": v(330.82, -203.97) * mm, "radius": 1.02 * mm});
            skCircle(sketch, "E80.1.1", {"center": v(330.82, -213.5) * mm, "radius": 1.02 * mm});
            skCircle(sketch, "E80.1.2", {"center": v(330.82, -410.35) * mm, "radius": 1.02 * mm});
            skCircle(sketch, "E80.1.3", {"center": v(330.82, -419.87) * mm, "radius": 1.02 * mm});
            skCircle(sketch, "E80.2.0", {"center": v(302.24, -448.45) * mm, "radius": 1.02 * mm});
            skCircle(sketch, "E80.2.1", {"center": v(292.72, -448.45) * mm, "radius": 1.02 * mm});
            skCircle(sketch, "E80.2.2", {"center": v(95.87, -448.45) * mm, "radius": 1.02 * mm});
            skCircle(sketch, "E80.2.3", {"center": v(86.34, -448.45) * mm, "radius": 1.02 * mm});
            skCircle(sketch, "E80.3.0", {"center": v(57.77, -419.87) * mm, "radius": 1.02 * mm});
            skCircle(sketch, "E80.3.1", {"center": v(57.77, -410.35) * mm, "radius": 1.02 * mm});
            skCircle(sketch, "E80.3.2", {"center": v(57.77, -213.5) * mm, "radius": 1.02 * mm});
            skCircle(sketch, "E80.3.3", {"center": v(57.77, -203.97) * mm, "radius": 1.02 * mm});
            skLineSegment(sketch, "E80.anchor1", {"start": v(194.3, -311.92) * mm, "end": v(86.34, -175.4) * mm, "construction": true});
            skLineSegment(sketch, "E80.anchor2", {"start": v(194.3, -311.92) * mm, "end": v(57.77, -419.87) * mm, "construction": true});
            skLineSegment(sketch, "E81.bottom", {"start": v(102.22, -219.85) * mm, "end": v(132.87, -219.85) * mm});
            skLineSegment(sketch, "E81.top", {"start": v(102.22, -250.5) * mm, "end": v(132.87, -250.5) * mm});
            skLineSegment(sketch, "E81.left", {"start": v(102.22, -219.85) * mm, "end": v(102.22, -250.5) * mm});
            skLineSegment(sketch, "E81.right", {"start": v(132.87, -219.85) * mm, "end": v(132.87, -250.5) * mm});
            skLineSegment(sketch, "E82.1.0", {"start": v(43.83, 115.88) * mm, "end": v(13.18, 115.88) * mm});
            skPoint(sketch, "E82.center", {"position": v(146.05, -134.62) * mm});
            skLineSegment(sketch, "E83.1.0", {"start": v(255.72, -404) * mm, "end": v(255.72, -373.35) * mm});
            skLineSegment(sketch, "E83.1.1", {"start": v(286.37, -404) * mm, "end": v(255.72, -404) * mm});
            skLineSegment(sketch, "E83.1.2", {"start": v(286.37, -404) * mm, "end": v(286.37, -373.35) * mm});
            skLineSegment(sketch, "E83.1.3", {"start": v(286.37, -373.35) * mm, "end": v(255.72, -373.35) * mm});
            skLineSegment(sketch, "E83.anchor1", {"start": v(194.3, -311.92) * mm, "end": v(132.87, -250.5) * mm, "construction": true});
            skLineSegment(sketch, "E83.anchor2", {"start": v(194.3, -311.92) * mm, "end": v(255.72, -373.35) * mm, "construction": true});
            skSolve(sketch);
        }
        {
            var Q0;
            Q0 = qSketchRegion(id + "F17", true);
            extrude(context, id + "F18", {"entities" : qUnion([Q0]), "depth" : (getVariable(context, 'T0')) * mm, "offsetDistance" : 25.4 * mm});
        }
        {
            var Q0;
            Q0=qCreatedBy(makeId("Top.planeOp"),FACE);
            var sketch = newSketch(context, id + "F19", { "sketchPlane" : qUnion([Q0])});
            skCircle(sketch, "E84.cCircle", {"center": v(162.42, 41.36) * mm, "radius": 3.97 * mm, "construction": true});
            skLineSegment(sketch, "E84.0", {"start": v(164.37, 44.82) * mm, "end": v(166.39, 41.4) * mm});
            skLineSegment(sketch, "E84.1", {"start": v(166.39, 41.4) * mm, "end": v(164.44, 37.94) * mm});
            skLineSegment(sketch, "E84.2", {"start": v(164.44, 37.94) * mm, "end": v(160.47, 37.9) * mm});
            skLineSegment(sketch, "E84.3", {"start": v(160.47, 37.9) * mm, "end": v(158.45, 41.32) * mm});
            skLineSegment(sketch, "E84.4", {"start": v(158.45, 41.32) * mm, "end": v(160.4, 44.78) * mm});
            skLineSegment(sketch, "E84.5", {"start": v(160.4, 44.78) * mm, "end": v(164.37, 44.82) * mm});
            skCircle(sketch, "E85.cCircle", {"center": v(192.94, 42.7) * mm, "radius": 3.97 * mm, "construction": true});
            skLineSegment(sketch, "E85.0", {"start": v(194.89, 46.15) * mm, "end": v(196.9, 42.73) * mm});
            skLineSegment(sketch, "E85.1", {"start": v(196.9, 42.73) * mm, "end": v(194.95, 39.27) * mm});
            skLineSegment(sketch, "E85.2", {"start": v(194.95, 39.27) * mm, "end": v(190.99, 39.23) * mm});
            skLineSegment(sketch, "E85.3", {"start": v(190.99, 39.23) * mm, "end": v(188.97, 42.65) * mm});
            skLineSegment(sketch, "E85.4", {"start": v(188.97, 42.65) * mm, "end": v(190.92, 46.1) * mm});
            skLineSegment(sketch, "E85.5", {"start": v(190.92, 46.1) * mm, "end": v(194.89, 46.15) * mm});
            skSolve(sketch);
        }
        {
            var Q0;
            Q0=makeQuery(id+"F19.imprint","IMPRINT",FACE,{"disambiguationData":[TD([[makeQuery(id+"F19.imprint","IMPRINT",EDGE,{"derivedFrom":sQuery(id+"F19.wireOp",EDGE,"E84.0")}),-1.0]])]});
            extrude(context, id + "F20", {"entities" : qUnion([Q0]), "depth" : 50.8 * mm, "offsetDistance" : 25.4 * mm});
        }
        {
            var Q0;
            Q0 = qSketchRegion(id + "F19", true);
            extrude(context, id + "F21", {"entities" : qUnion([Q0]), "depth" : 50.8 * mm, "offsetDistance" : 25.4 * mm});
        }
        {
            var Q0;
            Q0=makeQuery(id+"F21.opExtrude","CAP_FACE",FACE,{"disambiguationData":[OSD([sQuery(id+"F19.wireOp",EDGE,"E85.0"),sQuery(id+"F19.wireOp",EDGE,"E85.1"),sQuery(id+"F19.wireOp",EDGE,"E85.2"),sQuery(id+"F19.wireOp",EDGE,"E85.3"),sQuery(id+"F19.wireOp",EDGE,"E85.4"),sQuery(id+"F19.wireOp",EDGE,"E85.5")])],"isStart":false});
            extrude(context, id + "F22", {"entities" : qUnion([Q0]), "operationType" : NewBodyOperationType.ADD, "depth" : 25.4 * mm, "offsetDistance" : 25.4 * mm});
        }
        {
            var Q0;
            Q0=makeQuery(id+"F21.opExtrude","SWEPT_BODY",BODY,{"disambiguationData":[OSD([sQuery(id+"F19.wireOp",EDGE,"E84.0"),sQuery(id+"F19.wireOp",EDGE,"E84.1"),sQuery(id+"F19.wireOp",EDGE,"E84.2"),sQuery(id+"F19.wireOp",EDGE,"E84.3"),sQuery(id+"F19.wireOp",EDGE,"E84.4"),sQuery(id+"F19.wireOp",EDGE,"E84.5")])]});
            deleteBodies(context, id + "F23", {"entities" : qUnion([Q0])});
        }
        {
            var Q0;
            Q0=qCreatedBy(makeId("Top.planeOp"),FACE);
            var sketch = newSketch(context, id + "F24", { "sketchPlane" : qUnion([Q0])});
            skLineSegment(sketch, "E86.bottom", {"start": v(709.75, -19.37) * mm, "end": v(468.45, -19.37) * mm});
            skLineSegment(sketch, "E86.top", {"start": v(709.75, -311.47) * mm, "end": v(560.38, -311.47) * mm});
            skLineSegment(sketch, "E86.left", {"start": v(735.15, -44.77) * mm, "end": v(735.15, -286.07) * mm});
            skLineSegment(sketch, "E86.right", {"start": v(443.05, -44.77) * mm, "end": v(443.05, -286.07) * mm});
            skPoint(sketch, "E86.middle", {"position": v(589.1, -165.42) * mm});
            skPoint(sketch, "E87.visualSharp", {"position": v(443.05, -19.37) * mm});
            skArc(sketch, "E87.filletArc", {"start": v(468.45, -19.37) * mm, "mid": v(450.5, -26.81) * mm, "end": v(443.05, -44.77) * mm});
            skPoint(sketch, "E88.visualSharp", {"position": v(735.15, -19.37) * mm});
            skArc(sketch, "E88.filletArc", {"start": v(735.15, -44.77) * mm, "mid": v(727.71, -26.81) * mm, "end": v(709.75, -19.37) * mm});
            skPoint(sketch, "E89.visualSharp", {"position": v(735.15, -311.47) * mm});
            skArc(sketch, "E89.filletArc", {"start": v(709.75, -311.47) * mm, "mid": v(727.71, -304.03) * mm, "end": v(735.15, -286.07) * mm});
            skPoint(sketch, "E90.visualSharp", {"position": v(443.05, -311.47) * mm});
            skArc(sketch, "E90.filletArc", {"start": v(443.05, -286.07) * mm, "mid": v(450.5, -304.03) * mm, "end": v(468.45, -311.47) * mm});
            skLineSegment(sketch, "E91", {"start": v(589.1, -19.37) * mm, "end": v(589.1, -165.42) * mm, "construction": true});
            skLineSegment(sketch, "E92.bottom", {"start": v(595.45, -23.18) * mm, "end": v(582.75, -23.18) * mm});
            skLineSegment(sketch, "E92.top", {"start": v(595.45, -28.62) * mm, "end": v(582.75, -28.62) * mm});
            skLineSegment(sketch, "E92.left", {"start": v(595.45, -23.18) * mm, "end": v(595.45, -28.62) * mm});
            skLineSegment(sketch, "E92.right", {"start": v(582.75, -23.18) * mm, "end": v(582.75, -28.62) * mm});
            skPoint(sketch, "E92.middle", {"position": v(589.1, -25.9) * mm});
            skPoint(sketch, "E93.middle", {"position": v(589.1, -47.7) * mm});
            skLineSegment(sketch, "E94.bottom", {"start": v(595.45, -98.44) * mm, "end": v(582.75, -98.44) * mm});
            skLineSegment(sketch, "E94.top", {"start": v(595.45, -103.88) * mm, "end": v(582.75, -103.88) * mm});
            skLineSegment(sketch, "E94.left", {"start": v(595.45, -98.44) * mm, "end": v(595.45, -103.88) * mm});
            skLineSegment(sketch, "E94.right", {"start": v(582.75, -98.44) * mm, "end": v(582.75, -103.88) * mm});
            skPoint(sketch, "E94.middle", {"position": v(589.1, -101.16) * mm});
            skCircle(sketch, "E95", {"center": v(468.45, -44.77) * mm, "radius": 2.13 * mm});
            skCircle(sketch, "E96.1.0", {"center": v(709.75, -44.77) * mm, "radius": 2.13 * mm});
            skCircle(sketch, "E96.2.0", {"center": v(709.75, -286.07) * mm, "radius": 2.13 * mm});
            skCircle(sketch, "E96.3.0", {"center": v(468.45, -286.07) * mm, "radius": 2.13 * mm});
            skLineSegment(sketch, "E96.anchor1", {"start": v(589.1, -165.42) * mm, "end": v(468.45, -44.77) * mm, "construction": true});
            skLineSegment(sketch, "E96.anchor2", {"start": v(589.1, -165.42) * mm, "end": v(468.45, -286.07) * mm, "construction": true});
            skPoint(sketch, "E97.center", {"position": v(540.86, 16.12) * mm});
            skLineSegment(sketch, "E98.anchor1", {"start": v(589.1, -165.42) * mm, "end": v(527.68, -104) * mm, "construction": true});
            skLineSegment(sketch, "E99.bottom", {"start": v(493.85, -70.17) * mm, "end": v(530.84, -70.17) * mm});
            skLineSegment(sketch, "E99.top", {"start": v(493.85, -107.16) * mm, "end": v(530.84, -107.16) * mm});
            skLineSegment(sketch, "E99.left", {"start": v(493.85, -70.17) * mm, "end": v(493.85, -107.16) * mm});
            skLineSegment(sketch, "E99.right", {"start": v(530.84, -70.17) * mm, "end": v(530.84, -107.16) * mm});
            skPoint(sketch, "E100.1.0", {"position": v(449.58, -165.42) * mm});
            skLineSegment(sketch, "E100.1.1", {"start": v(443.05, -165.42) * mm, "end": v(589.1, -165.42) * mm, "construction": true});
            skPoint(sketch, "E100.1.2", {"position": v(471.37, -165.42) * mm});
            skPoint(sketch, "E100.1.3", {"position": v(524.84, -165.42) * mm});
            skLineSegment(sketch, "E100.1.4", {"start": v(522.12, -171.77) * mm, "end": v(527.56, -171.77) * mm});
            skLineSegment(sketch, "E100.1.5", {"start": v(446.86, -171.77) * mm, "end": v(452.3, -171.77) * mm});
            skLineSegment(sketch, "E100.1.6", {"start": v(452.3, -159.07) * mm, "end": v(452.3, -171.77) * mm});
            skLineSegment(sketch, "E100.1.7", {"start": v(446.86, -159.07) * mm, "end": v(446.86, -171.77) * mm});
            skLineSegment(sketch, "E100.1.8", {"start": v(522.12, -159.07) * mm, "end": v(522.12, -171.77) * mm});
            skLineSegment(sketch, "E100.1.9", {"start": v(522.12, -159.07) * mm, "end": v(527.56, -159.07) * mm});
            skLineSegment(sketch, "E100.1.10", {"start": v(527.56, -159.07) * mm, "end": v(527.56, -171.77) * mm});
            skLineSegment(sketch, "E100.1.11", {"start": v(446.86, -159.07) * mm, "end": v(452.3, -159.07) * mm});
            skPoint(sketch, "E100.2.0", {"position": v(589.1, -304.94) * mm});
            skLineSegment(sketch, "E100.2.1", {"start": v(589.1, -311.47) * mm, "end": v(589.1, -165.42) * mm, "construction": true});
            skPoint(sketch, "E100.2.2", {"position": v(589.1, -283.15) * mm});
            skPoint(sketch, "E100.2.3", {"position": v(589.1, -229.68) * mm});
            skLineSegment(sketch, "E100.2.4", {"start": v(595.45, -232.4) * mm, "end": v(595.45, -226.97) * mm});
            skLineSegment(sketch, "E100.2.5", {"start": v(595.45, -307.66) * mm, "end": v(595.45, -302.23) * mm});
            skLineSegment(sketch, "E100.2.6", {"start": v(582.75, -302.23) * mm, "end": v(595.45, -302.23) * mm});
            skLineSegment(sketch, "E100.2.7", {"start": v(582.75, -307.66) * mm, "end": v(595.45, -307.66) * mm});
            skLineSegment(sketch, "E100.2.8", {"start": v(582.75, -232.4) * mm, "end": v(595.45, -232.4) * mm});
            skLineSegment(sketch, "E100.2.9", {"start": v(582.75, -232.4) * mm, "end": v(582.75, -226.97) * mm});
            skLineSegment(sketch, "E100.2.10", {"start": v(582.75, -226.97) * mm, "end": v(595.45, -226.97) * mm});
            skLineSegment(sketch, "E100.2.11", {"start": v(582.75, -307.66) * mm, "end": v(582.75, -302.23) * mm});
            skPoint(sketch, "E100.3.0", {"position": v(728.62, -165.42) * mm});
            skLineSegment(sketch, "E100.3.1", {"start": v(735.15, -165.42) * mm, "end": v(589.1, -165.42) * mm, "construction": true});
            skPoint(sketch, "E100.3.2", {"position": v(706.83, -165.42) * mm});
            skPoint(sketch, "E100.3.3", {"position": v(653.36, -165.42) * mm});
            skLineSegment(sketch, "E100.3.4", {"start": v(656.08, -159.07) * mm, "end": v(650.65, -159.07) * mm});
            skLineSegment(sketch, "E100.3.5", {"start": v(731.34, -159.07) * mm, "end": v(725.9, -159.07) * mm});
            skLineSegment(sketch, "E100.3.6", {"start": v(725.9, -171.77) * mm, "end": v(725.9, -159.07) * mm});
            skLineSegment(sketch, "E100.3.7", {"start": v(731.34, -171.77) * mm, "end": v(731.34, -159.07) * mm});
            skLineSegment(sketch, "E100.3.8", {"start": v(656.08, -171.77) * mm, "end": v(656.08, -159.07) * mm});
            skLineSegment(sketch, "E100.3.9", {"start": v(656.08, -171.77) * mm, "end": v(650.65, -171.77) * mm});
            skLineSegment(sketch, "E100.3.10", {"start": v(650.65, -171.77) * mm, "end": v(650.65, -159.07) * mm});
            skLineSegment(sketch, "E100.3.11", {"start": v(731.34, -171.77) * mm, "end": v(725.9, -171.77) * mm});
            skLineSegment(sketch, "E101.1.0", {"start": v(684.35, -260.67) * mm, "end": v(684.35, -223.68) * mm});
            skLineSegment(sketch, "E101.1.1", {"start": v(684.35, -260.67) * mm, "end": v(647.36, -260.67) * mm});
            skLineSegment(sketch, "E101.1.2", {"start": v(647.36, -260.67) * mm, "end": v(647.36, -223.68) * mm});
            skLineSegment(sketch, "E101.1.3", {"start": v(684.35, -223.68) * mm, "end": v(647.36, -223.68) * mm});
            skCircle(sketch, "E102", {"center": v(547.97, -272.44) * mm, "radius": 1.59 * mm});
            skCircle(sketch, "E103", {"center": v(542.9, -220.37) * mm, "radius": 1.59 * mm});
            skCircle(sketch, "E104", {"center": v(514.95, -220.37) * mm, "radius": 1.59 * mm});
            skCircle(sketch, "E105", {"center": v(499.71, -271.17) * mm, "radius": 1.59 * mm});
            skLineSegment(sketch, "E106.bottom", {"start": v(664.03, -141.3) * mm, "end": v(664.03, -189.55) * mm, "construction": true});
            skLineSegment(sketch, "E106.top", {"start": v(514.17, -141.3) * mm, "end": v(514.17, -189.55) * mm, "construction": true});
            skLineSegment(sketch, "E106.left", {"start": v(664.03, -141.3) * mm, "end": v(514.17, -141.3) * mm, "construction": true});
            skLineSegment(sketch, "E106.right", {"start": v(664.03, -189.55) * mm, "end": v(595.45, -189.55) * mm, "construction": true});
            skLineSegment(sketch, "E107.bottom", {"start": v(514.17, -159.07) * mm, "end": v(509.12, -159.07) * mm});
            skLineSegment(sketch, "E107.top", {"start": v(514.17, -171.77) * mm, "end": v(509.12, -171.77) * mm});
            skLineSegment(sketch, "E107.left", {"start": v(514.17, -159.07) * mm, "end": v(514.17, -171.77) * mm});
            skLineSegment(sketch, "E107.right", {"start": v(509.12, -159.07) * mm, "end": v(509.12, -171.77) * mm});
            skPoint(sketch, "E107.middle", {"position": v(511.64, -165.42) * mm});
            skLineSegment(sketch, "E108.bottom", {"start": v(664.03, -159.07) * mm, "end": v(669.09, -159.07) * mm});
            skLineSegment(sketch, "E108.top", {"start": v(664.03, -171.77) * mm, "end": v(669.09, -171.77) * mm});
            skLineSegment(sketch, "E108.left", {"start": v(664.03, -159.07) * mm, "end": v(664.03, -171.77) * mm});
            skLineSegment(sketch, "E108.right", {"start": v(669.09, -159.07) * mm, "end": v(669.09, -171.77) * mm});
            skPoint(sketch, "E108.middle", {"position": v(666.56, -165.42) * mm});
            skLineSegment(sketch, "E109.bottom", {"start": v(595.45, -141.3) * mm, "end": v(582.75, -141.3) * mm});
            skLineSegment(sketch, "E109.top", {"start": v(595.45, -136.24) * mm, "end": v(582.75, -136.24) * mm});
            skLineSegment(sketch, "E109.left", {"start": v(595.45, -141.3) * mm, "end": v(595.45, -136.24) * mm});
            skLineSegment(sketch, "E109.right", {"start": v(582.75, -141.3) * mm, "end": v(582.75, -136.24) * mm});
            skPoint(sketch, "E109.middle", {"position": v(589.1, -138.76) * mm});
            skLineSegment(sketch, "E110.bottom", {"start": v(595.45, -189.55) * mm, "end": v(582.75, -189.55) * mm});
            skLineSegment(sketch, "E110.top", {"start": v(595.45, -194.6) * mm, "end": v(582.75, -194.6) * mm});
            skLineSegment(sketch, "E110.left", {"start": v(595.45, -189.55) * mm, "end": v(595.45, -194.6) * mm});
            skLineSegment(sketch, "E110.right", {"start": v(582.75, -189.55) * mm, "end": v(582.75, -194.6) * mm});
            skPoint(sketch, "E110.middle", {"position": v(589.1, -192.08) * mm});
            skLineSegment(sketch, "E111.trimOffspring", {"start": v(582.75, -189.55) * mm, "end": v(514.17, -189.55) * mm, "construction": true});
            skLineSegment(sketch, "E112.top", {"start": v(530.9, -298.95) * mm, "end": v(560.38, -298.95) * mm});
            skLineSegment(sketch, "E112.left", {"start": v(530.9, -311.47) * mm, "end": v(530.9, -298.95) * mm});
            skLineSegment(sketch, "E112.right", {"start": v(560.38, -311.47) * mm, "end": v(560.38, -298.95) * mm});
            skLineSegment(sketch, "E113.trimOffspring", {"start": v(530.9, -311.47) * mm, "end": v(468.45, -311.47) * mm});
            skSolve(sketch);
        }
        {
            var Q0;
            Q0=makeQuery(id+"F24.imprint","IMPRINT",FACE,{"disambiguationData":[TD([[makeQuery(id+"F24.imprint","IMPRINT",EDGE,{"derivedFrom":sQuery(id+"F24.wireOp",EDGE,"E86.bottom")}),1.0]])]});
            extrude(context, id + "F25", {"entities" : qUnion([Q0]), "depth" : (getVariable(context, 'T0')) * mm, "offsetDistance" : 25.4 * mm});
        }
        {
            var Q0;
            Q0=qCreatedBy(makeId("Top.planeOp"),FACE);
            var sketch = newSketch(context, id + "F26", { "sketchPlane" : qUnion([Q0])});
            skLineSegment(sketch, "E114.bottom", {"start": v(283.23, -33.54) * mm, "end": v(257.83, -33.54) * mm});
            skLineSegment(sketch, "E114.top", {"start": v(289.58, -58.94) * mm, "end": v(276.88, -58.94) * mm});
            skLineSegment(sketch, "E114.left", {"start": v(289.58, -39.9) * mm, "end": v(289.58, -58.94) * mm});
            skLineSegment(sketch, "E114.right", {"start": v(251.48, -39.9) * mm, "end": v(251.48, -58.94) * mm});
            skPoint(sketch, "E114.middle", {"position": v(270.53, -46.24) * mm});
            skPoint(sketch, "E115.endSnap0", {"position": v(270.53, -58.94) * mm});
            skLineSegment(sketch, "E116.top", {"start": v(276.88, -64.38) * mm, "end": v(264.18, -64.38) * mm});
            skLineSegment(sketch, "E116.left", {"start": v(276.88, -58.94) * mm, "end": v(276.88, -64.38) * mm});
            skLineSegment(sketch, "E116.right", {"start": v(264.18, -58.94) * mm, "end": v(264.18, -64.38) * mm});
            skPoint(sketch, "E116.middle", {"position": v(270.53, -61.66) * mm});
            skLineSegment(sketch, "E117.trimOffspring", {"start": v(264.18, -58.94) * mm, "end": v(251.48, -58.94) * mm});
            skLineSegment(sketch, "E118", {"start": v(270.53, -33.54) * mm, "end": v(270.53, -64.38) * mm, "construction": true});
            skPoint(sketch, "E119.visualSharp", {"position": v(251.48, -33.54) * mm});
            skArc(sketch, "E119.filletArc", {"start": v(257.83, -33.54) * mm, "mid": v(253.34, -35.4) * mm, "end": v(251.48, -39.9) * mm});
            skPoint(sketch, "E120.visualSharp", {"position": v(289.58, -33.54) * mm});
            skArc(sketch, "E120.filletArc", {"start": v(289.58, -39.9) * mm, "mid": v(287.72, -35.4) * mm, "end": v(283.23, -33.54) * mm});
            skSolve(sketch);
        }
        {
            var Q0;
            Q0=makeQuery(id+"F26.imprint","IMPRINT",FACE,{"disambiguationData":[TD([[makeQuery(id+"F26.imprint","IMPRINT",EDGE,{"derivedFrom":sQuery(id+"F26.wireOp",EDGE,"E114.bottom")}),1.0]])]});
            extrude(context, id + "F27", {"entities" : qUnion([Q0]), "depth" : (getVariable(context, 'T0')) * mm, "offsetDistance" : 25.4 * mm});
        }
        {
            var Q0;
            Q0=qCreatedBy(makeId("Top.planeOp"),FACE);
            var sketch = newSketch(context, id + "F28", { "sketchPlane" : qUnion([Q0])});
            skLineSegment(sketch, "E121.bottom", {"start": v(689.25, 371.05) * mm, "end": v(447.95, 371.05) * mm});
            skLineSegment(sketch, "E121.top", {"start": v(689.25, 78.95) * mm, "end": v(447.95, 78.95) * mm});
            skLineSegment(sketch, "E121.left", {"start": v(714.65, 345.65) * mm, "end": v(714.65, 104.35) * mm});
            skLineSegment(sketch, "E121.right", {"start": v(422.55, 345.65) * mm, "end": v(422.55, 104.35) * mm});
            skPoint(sketch, "E122.visualSharp", {"position": v(422.55, 371.05) * mm});
            skArc(sketch, "E122.filletArc", {"start": v(447.95, 371.05) * mm, "mid": v(430, 363.61) * mm, "end": v(422.55, 345.65) * mm});
            skPoint(sketch, "E123.visualSharp", {"position": v(714.65, 371.05) * mm});
            skArc(sketch, "E123.filletArc", {"start": v(714.65, 345.65) * mm, "mid": v(707.22, 363.61) * mm, "end": v(689.25, 371.05) * mm});
            skPoint(sketch, "E124.visualSharp", {"position": v(714.65, 78.95) * mm});
            skArc(sketch, "E124.filletArc", {"start": v(689.25, 78.95) * mm, "mid": v(707.22, 86.4) * mm, "end": v(714.65, 104.35) * mm});
            skPoint(sketch, "E125.visualSharp", {"position": v(422.55, 78.95) * mm});
            skArc(sketch, "E125.filletArc", {"start": v(422.55, 104.35) * mm, "mid": v(430, 86.4) * mm, "end": v(447.95, 78.95) * mm});
            skCircle(sketch, "E126", {"center": v(447.95, 345.65) * mm, "radius": 2.13 * mm});
            skCircle(sketch, "E127.1.0", {"center": v(689.25, 345.65) * mm, "radius": 2.13 * mm});
            skCircle(sketch, "E127.2.0", {"center": v(689.25, 104.35) * mm, "radius": 2.13 * mm});
            skCircle(sketch, "E127.3.0", {"center": v(447.95, 104.35) * mm, "radius": 2.13 * mm});
            skLineSegment(sketch, "E127.anchor1", {"start": v(568.6, 225) * mm, "end": v(447.95, 345.65) * mm, "construction": true});
            skLineSegment(sketch, "E127.anchor2", {"start": v(568.6, 225) * mm, "end": v(447.95, 104.35) * mm, "construction": true});
            skPoint(sketch, "E128.center", {"position": v(525.54, 404.18) * mm});
            skLineSegment(sketch, "E129.2.1", {"start": v(573.79, 76.6) * mm, "end": v(573.79, 222.64) * mm, "construction": true});
            skLineSegment(sketch, "E129.3.1", {"start": v(719.84, 222.64) * mm, "end": v(573.79, 222.64) * mm, "construction": true});
            skLineSegment(sketch, "E130", {"start": v(568.6, 225) * mm, "end": v(568.6, 371.05) * mm, "construction": true});
            skLineSegment(sketch, "E131.bottom", {"start": v(600.35, 324.06) * mm, "end": v(605.4, 324.06) * mm});
            skLineSegment(sketch, "E131.top", {"start": v(600.35, 311.36) * mm, "end": v(605.4, 311.36) * mm});
            skLineSegment(sketch, "E131.left", {"start": v(600.35, 324.06) * mm, "end": v(600.35, 311.36) * mm});
            skLineSegment(sketch, "E131.right", {"start": v(605.4, 324.06) * mm, "end": v(605.4, 311.36) * mm});
            skLineSegment(sketch, "E132.MirrorCS", {"start": v(536.85, 324.06) * mm, "end": v(531.8, 324.06) * mm});
            skLineSegment(sketch, "E133.MirrorCS", {"start": v(536.85, 311.36) * mm, "end": v(531.8, 311.36) * mm});
            skLineSegment(sketch, "E134.MirrorCS", {"start": v(536.85, 324.06) * mm, "end": v(536.85, 311.36) * mm});
            skLineSegment(sketch, "E135.MirrorCS", {"start": v(531.8, 324.06) * mm, "end": v(531.8, 311.36) * mm});
            skLineSegment(sketch, "E136.bottom", {"start": v(605.4, 260.56) * mm, "end": v(600.35, 260.56) * mm});
            skLineSegment(sketch, "E136.top", {"start": v(605.4, 273.26) * mm, "end": v(600.35, 273.26) * mm});
            skLineSegment(sketch, "E136.left", {"start": v(605.4, 260.56) * mm, "end": v(605.4, 273.26) * mm});
            skLineSegment(sketch, "E136.right", {"start": v(600.35, 260.56) * mm, "end": v(600.35, 273.26) * mm});
            skLineSegment(sketch, "E137.MirrorCS", {"start": v(531.8, 273.26) * mm, "end": v(536.85, 273.26) * mm});
            skLineSegment(sketch, "E138.MirrorCS", {"start": v(531.8, 260.56) * mm, "end": v(536.85, 260.56) * mm});
            skLineSegment(sketch, "E139.MirrorCS", {"start": v(536.85, 260.56) * mm, "end": v(536.85, 273.26) * mm});
            skLineSegment(sketch, "E140.MirrorCS", {"start": v(531.8, 260.56) * mm, "end": v(531.8, 273.26) * mm});
            skCircle(sketch, "E141", {"center": v(662.24, 330.83) * mm, "radius": 12.7 * mm});
            skCircle(sketch, "E142", {"center": v(540.07, 118.33) * mm, "radius": 1.59 * mm});
            skCircle(sketch, "E143", {"center": v(534.99, 170.4) * mm, "radius": 1.59 * mm});
            skCircle(sketch, "E144", {"center": v(507.05, 170.4) * mm, "radius": 1.59 * mm});
            skCircle(sketch, "E145", {"center": v(491.8, 119.6) * mm, "radius": 1.59 * mm});
            skCircle(sketch, "E146", {"center": v(464.59, 152.74) * mm, "radius": 12.7 * mm});
            skCircle(sketch, "E147.1.0", {"center": v(645.58, 275.22) * mm, "radius": 1.46 * mm});
            skCircle(sketch, "E147.1.1", {"center": v(682.58, 275.22) * mm, "radius": 1.46 * mm});
            skCircle(sketch, "E147.1.2", {"center": v(682.58, 312.22) * mm, "radius": 1.46 * mm});
            skCircle(sketch, "E147.1.3", {"center": v(645.58, 312.22) * mm, "radius": 1.46 * mm});
            skLineSegment(sketch, "E148.1.0", {"start": v(648.76, 278.4) * mm, "end": v(648.76, 309.04) * mm});
            skLineSegment(sketch, "E148.1.1", {"start": v(679.4, 278.4) * mm, "end": v(648.76, 278.4) * mm});
            skLineSegment(sketch, "E148.1.2", {"start": v(679.4, 278.4) * mm, "end": v(679.4, 309.04) * mm});
            skLineSegment(sketch, "E148.1.3", {"start": v(679.4, 309.04) * mm, "end": v(648.76, 309.04) * mm});
            skLineSegment(sketch, "E149.bottom", {"start": v(624.46, 298.2) * mm, "end": v(611.76, 298.2) * mm});
            skLineSegment(sketch, "E149.top", {"start": v(624.46, 292.77) * mm, "end": v(611.76, 292.77) * mm});
            skLineSegment(sketch, "E149.left", {"start": v(624.46, 298.2) * mm, "end": v(624.46, 292.77) * mm});
            skLineSegment(sketch, "E149.right", {"start": v(611.76, 298.2) * mm, "end": v(611.76, 292.77) * mm});
            skPoint(sketch, "E149.middle", {"position": v(618.1, 295.49) * mm});
            skLineSegment(sketch, "E150.MirrorCS", {"start": v(512.75, 292.77) * mm, "end": v(525.45, 292.77) * mm});
            skPoint(sketch, "E151.MirrorP", {"position": v(519.1, 295.49) * mm});
            skLineSegment(sketch, "E152.MirrorCS", {"start": v(512.75, 298.2) * mm, "end": v(512.75, 292.77) * mm});
            skLineSegment(sketch, "E153.MirrorCS", {"start": v(512.75, 298.2) * mm, "end": v(525.45, 298.2) * mm});
            skLineSegment(sketch, "E154.MirrorCS", {"start": v(525.45, 298.2) * mm, "end": v(525.45, 292.77) * mm});
            skSolve(sketch);
        }
        {
            var Q0;
            Q0=qCreatedBy(makeId("Top.planeOp"),FACE);
            var sketch = newSketch(context, id + "F29", { "sketchPlane" : qUnion([Q0])});
            skCircle(sketch, "E155", {"center": v(-278.25, -195.17) * mm, "radius": 25.4 * mm});
            skCircle(sketch, "E156", {"center": v(-278.25, -195.17) * mm, "radius": 29.21 * mm});
            skLineSegment(sketch, "E157", {"start": v(-278.25, -195.17) * mm, "end": v(-278.25, -271.37) * mm, "construction": true});
            skLineSegment(sketch, "E158", {"start": v(-278.25, -271.37) * mm, "end": v(-316.02, -271.37) * mm, "construction": true});
            skSolve(sketch);
        }
        {
            var Q0;
            Q0 = qSketchRegion(id + "F29", true);
            var Q1;
            Q1=sQuery(id+"F29.wireOp",EDGE,"E158");
            revolve(context, id + "F30", {"entities" : qUnion([Q0]), "axis" : qUnion([Q1]), "revolveType" : RevolveType.ONE_DIRECTION, "angle" : 50 * degree});
        }
        {
            var Q0;
            Q0=makeQuery(id+"F30.opRevolve","CAP_FACE",FACE,{"disambiguationData":[OSD([sQuery(id+"F29.wireOp",EDGE,"E155"),sQuery(id+"F29.wireOp",EDGE,"E156")])],"isStart":true});
            var sketch = newSketch(context, id + "F31", { "sketchPlane" : qUnion([Q0])});
            skLineSegment(sketch, "E159.bottom", {"start": v(-297.3, -210.41) * mm, "end": v(-259.2, -210.41) * mm});
            skLineSegment(sketch, "E159.top", {"start": v(-297.3, -273.91) * mm, "end": v(-259.2, -273.91) * mm});
            skLineSegment(sketch, "E159.left", {"start": v(-297.3, -210.41) * mm, "end": v(-297.3, -273.91) * mm});
            skLineSegment(sketch, "E159.right", {"start": v(-259.2, -210.41) * mm, "end": v(-259.2, -273.91) * mm});
            skSolve(sketch);
        }
        {
            var Q0;
            Q0 = qSketchRegion(id + "F31", true);
            extrude(context, id + "F32", {"entities" : qUnion([Q0]), "operationType" : NewBodyOperationType.REMOVE, "oppositeDirection" : true, "depth" : 63.5 * mm, "offsetDistance" : 25.4 * mm});
        }
        {
            var Q0;
            Q0=qCreatedBy(makeId("Right.planeOp"),FACE);
            var sketch = newSketch(context, id + "F33", { "sketchPlane" : qUnion([Q0])});
            skLineSegment(sketch, "E160.bottom", {"start": v(-162.89, 29.27) * mm, "end": v(-251.79, 29.27) * mm});
            skLineSegment(sketch, "E160.left", {"start": v(-162.89, 16.57) * mm, "end": v(-162.89, -21.53) * mm});
            skLineSegment(sketch, "E160.right", {"start": v(-277.19, 3.87) * mm, "end": v(-277.19, -8.83) * mm});
            skCircle(sketch, "E161", {"center": v(-188.29, -2.6) * mm, "radius": 2.13 * mm});
            skPoint(sketch, "E161.centerSnap0", {"position": v(-277.19, -2.6) * mm});
            skLineSegment(sketch, "E162.bottom", {"start": v(-162.89, 29.27) * mm, "end": v(-157.45, 29.27) * mm});
            skLineSegment(sketch, "E162.top", {"start": v(-162.89, 16.57) * mm, "end": v(-157.45, 16.57) * mm});
            skLineSegment(sketch, "E162.right", {"start": v(-157.45, 29.27) * mm, "end": v(-157.45, 16.57) * mm});
            skLineSegment(sketch, "E163.bottom", {"start": v(-162.89, -34.23) * mm, "end": v(-157.45, -34.23) * mm});
            skLineSegment(sketch, "E163.top", {"start": v(-162.89, -21.53) * mm, "end": v(-157.45, -21.53) * mm});
            skLineSegment(sketch, "E163.right", {"start": v(-157.45, -34.23) * mm, "end": v(-157.45, -21.53) * mm});
            skPoint(sketch, "E164.visualSharp", {"position": v(-277.19, 29.27) * mm});
            skArc(sketch, "E164.filletArc", {"start": v(-251.79, 29.27) * mm, "mid": v(-269.75, 21.83) * mm, "end": v(-277.19, 3.87) * mm});
            skPoint(sketch, "E165.visualSharp", {"position": v(-277.19, -34.46) * mm});
            skLineSegment(sketch, "E166", {"start": v(-190.42, -2.6) * mm, "end": v(-277.19, -2.6) * mm, "construction": true});
            skLineSegment(sketch, "E167", {"start": v(-240.36, 2.4) * mm, "end": v(-252.36, 2.4) * mm});
            skArc(sketch, "E168", {"start": v(-240.36, 2.4) * mm, "mid": v(-236.82, 0.94) * mm, "end": v(-235.36, -2.6) * mm});
            skArc(sketch, "E169", {"start": v(-252.36, 2.4) * mm, "mid": v(-255.9, 0.94) * mm, "end": v(-257.36, -2.6) * mm});
            skCircle(sketch, "E170", {"center": v(-240.36, 5.4) * mm, "radius": 1.3 * mm});
            skCircle(sketch, "E171.1.0.0", {"center": v(-243.36, 5.4) * mm, "radius": 1.3 * mm});
            skCircle(sketch, "E171.2.0.0", {"center": v(-246.36, 5.4) * mm, "radius": 1.3 * mm});
            skCircle(sketch, "E171.3.0.0", {"center": v(-249.36, 5.4) * mm, "radius": 1.3 * mm});
            skCircle(sketch, "E171.4.0.0", {"center": v(-252.36, 5.4) * mm, "radius": 1.3 * mm});
            skLineSegment(sketch, "E171.direction1", {"start": v(-240.36, 5.4) * mm, "end": v(-243.36, 5.4) * mm, "construction": true});
            skArc(sketch, "E172.MirrorCS", {"start": v(-240.36, -7.6) * mm, "mid": v(-236.82, -6.13) * mm, "end": v(-235.36, -2.6) * mm});
            skLineSegment(sketch, "E173.MirrorCS", {"start": v(-240.36, -7.6) * mm, "end": v(-252.36, -7.6) * mm});
            skArc(sketch, "E174.MirrorCS", {"start": v(-252.36, -7.6) * mm, "mid": v(-255.9, -6.13) * mm, "end": v(-257.36, -2.6) * mm});
            skLineSegment(sketch, "E175.bottom", {"start": v(-169.24, 0) * mm, "end": v(-181.94, 0) * mm});
            skLineSegment(sketch, "E175.top", {"start": v(-169.24, -5.18) * mm, "end": v(-181.94, -5.18) * mm});
            skLineSegment(sketch, "E175.left", {"start": v(-169.24, 0) * mm, "end": v(-169.24, -5.18) * mm});
            skLineSegment(sketch, "E175.right", {"start": v(-181.94, 0) * mm, "end": v(-181.94, -5.18) * mm});
            skPoint(sketch, "E175.middle", {"position": v(-175.59, -2.6) * mm});
            skLineSegment(sketch, "E176.top", {"start": v(-251.79, -70.28) * mm, "end": v(-162.89, -70.28) * mm});
            skLineSegment(sketch, "E176.left", {"start": v(-277.19, -8.83) * mm, "end": v(-277.19, -44.88) * mm});
            skLineSegment(sketch, "E176.right", {"start": v(-162.89, -34.23) * mm, "end": v(-162.89, -70.28) * mm});
            skLineSegment(sketch, "E177.MirrorCS", {"start": v(-240.36, -10.6) * mm, "end": v(-243.36, -10.6) * mm, "construction": true});
            skCircle(sketch, "E178.MirrorC", {"center": v(-243.36, -10.6) * mm, "radius": 1.3 * mm});
            skCircle(sketch, "E179.MirrorC", {"center": v(-246.36, -10.6) * mm, "radius": 1.3 * mm});
            skCircle(sketch, "E180.MirrorC", {"center": v(-249.36, -10.6) * mm, "radius": 1.3 * mm});
            skCircle(sketch, "E181.MirrorC", {"center": v(-240.36, -10.6) * mm, "radius": 1.3 * mm});
            skCircle(sketch, "E182.MirrorC", {"center": v(-252.36, -10.6) * mm, "radius": 1.3 * mm});
            skLineSegment(sketch, "E183.bottom", {"start": v(-258.14, -40.7) * mm, "end": v(-237.82, -40.7) * mm});
            skLineSegment(sketch, "E183.top", {"start": v(-258.14, -49.07) * mm, "end": v(-237.82, -49.07) * mm});
            skLineSegment(sketch, "E183.left", {"start": v(-258.14, -40.7) * mm, "end": v(-258.14, -49.07) * mm});
            skLineSegment(sketch, "E183.right", {"start": v(-237.82, -40.7) * mm, "end": v(-237.82, -49.07) * mm});
            skCircle(sketch, "E184", {"center": v(-236.55, -44.88) * mm, "radius": 0.9 * mm});
            skLineSegment(sketch, "E185", {"start": v(-258.14, -44.88) * mm, "end": v(-232.1, -44.88) * mm, "construction": true});
            skCircle(sketch, "E186", {"center": v(-259.4, -44.88) * mm, "radius": 0.89 * mm});
            skCircle(sketch, "E187", {"center": v(-241.63, -34.09) * mm, "radius": 1.3 * mm});
            skCircle(sketch, "E188.MirrorC", {"center": v(-241.63, -55.68) * mm, "radius": 1.3 * mm});
            skPoint(sketch, "E189.visualSharp", {"position": v(-277.19, -70.28) * mm});
            skArc(sketch, "E189.filletArc", {"start": v(-277.19, -44.88) * mm, "mid": v(-269.75, -62.84) * mm, "end": v(-251.79, -70.28) * mm});
            skSolve(sketch);
        }
        {
            var Q0;
            Q0 = qSketchRegion(id + "F33", true);
            extrude(context, id + "F34", {"entities" : qUnion([Q0]), "operationType" : NewBodyOperationType.ADD, "depth" : (getVariable(context, 'T0')) * mm, "offsetDistance" : 25.4 * mm});
        }
        {
            var Q0;
            Q0=qCreatedBy(makeId("Top.planeOp"),FACE);
            var sketch = newSketch(context, id + "F35", { "sketchPlane" : qUnion([Q0])});
            skLineSegment(sketch, "E190.bottom", {"start": v(-104.17, -272.95) * mm, "end": v(-193.07, -272.95) * mm});
            skLineSegment(sketch, "E190.left", {"start": v(-104.17, -285.65) * mm, "end": v(-104.17, -323.75) * mm});
            skLineSegment(sketch, "E190.right", {"start": v(-218.47, -298.35) * mm, "end": v(-218.47, -311.05) * mm});
            skCircle(sketch, "E191", {"center": v(-129.57, -304.58) * mm, "radius": 2.13 * mm});
            skPoint(sketch, "E191.centerSnap0", {"position": v(-218.47, -304.58) * mm});
            skLineSegment(sketch, "E192.bottom", {"start": v(-104.17, -272.95) * mm, "end": v(-98.74, -272.95) * mm});
            skLineSegment(sketch, "E192.top", {"start": v(-104.17, -285.65) * mm, "end": v(-98.74, -285.65) * mm});
            skLineSegment(sketch, "E192.right", {"start": v(-98.74, -272.95) * mm, "end": v(-98.74, -285.65) * mm});
            skLineSegment(sketch, "E193.bottom", {"start": v(-104.17, -336.45) * mm, "end": v(-98.74, -336.45) * mm});
            skLineSegment(sketch, "E193.top", {"start": v(-104.17, -323.75) * mm, "end": v(-98.74, -323.75) * mm});
            skLineSegment(sketch, "E193.right", {"start": v(-98.74, -336.45) * mm, "end": v(-98.74, -323.75) * mm});
            skPoint(sketch, "E194.visualSharp", {"position": v(-218.47, -272.95) * mm});
            skArc(sketch, "E194.filletArc", {"start": v(-193.07, -272.95) * mm, "mid": v(-211.03, -280.39) * mm, "end": v(-218.47, -298.35) * mm});
            skPoint(sketch, "E195.visualSharp", {"position": v(-218.47, -336.22) * mm});
            skLineSegment(sketch, "E196", {"start": v(-129.57, -304.58) * mm, "end": v(-218.47, -304.58) * mm, "construction": true});
            skArc(sketch, "E197", {"start": v(-175.52, -308.09) * mm, "mid": v(-170.21, -304.58) * mm, "end": v(-175.52, -301.08) * mm});
            skArc(sketch, "E198.1.0.0", {"start": v(-175.52, -301.08) * mm, "mid": v(-177.02, -300.77) * mm, "end": v(-178.52, -301.08) * mm});
            skArc(sketch, "E198.2.0.0", {"start": v(-178.52, -301.08) * mm, "mid": v(-180.02, -300.77) * mm, "end": v(-181.52, -301.08) * mm});
            skArc(sketch, "E198.3.0.0", {"start": v(-181.52, -301.08) * mm, "mid": v(-183.02, -300.77) * mm, "end": v(-184.52, -301.08) * mm});
            skArc(sketch, "E198.4.0.0", {"start": v(-184.52, -301.08) * mm, "mid": v(-189.83, -304.58) * mm, "end": v(-184.52, -308.09) * mm});
            skLineSegment(sketch, "E198.direction1", {"start": v(-174.02, -304.58) * mm, "end": v(-177.02, -304.58) * mm, "construction": true});
            skArc(sketch, "E199.trimOffspring", {"start": v(-178.52, -308.09) * mm, "mid": v(-177.02, -308.4) * mm, "end": v(-175.52, -308.09) * mm});
            skArc(sketch, "E200.trimOffspring", {"start": v(-181.52, -308.09) * mm, "mid": v(-180.02, -308.4) * mm, "end": v(-178.52, -308.09) * mm});
            skArc(sketch, "E201.trimOffspring", {"start": v(-184.52, -308.09) * mm, "mid": v(-183.02, -308.4) * mm, "end": v(-181.52, -308.09) * mm});
            skLineSegment(sketch, "E202.bottom", {"start": v(-123.22, -302) * mm, "end": v(-110.52, -302) * mm});
            skLineSegment(sketch, "E202.top", {"start": v(-123.22, -307.17) * mm, "end": v(-110.52, -307.17) * mm});
            skLineSegment(sketch, "E202.left", {"start": v(-123.22, -302) * mm, "end": v(-123.22, -307.17) * mm});
            skLineSegment(sketch, "E202.right", {"start": v(-110.52, -302) * mm, "end": v(-110.52, -307.17) * mm});
            skPoint(sketch, "E202.middle", {"position": v(-116.87, -304.58) * mm});
            skLineSegment(sketch, "E203", {"start": v(-218.47, -311.05) * mm, "end": v(-218.47, -346.87) * mm});
            skLineSegment(sketch, "E204", {"start": v(-193.07, -372.27) * mm, "end": v(-104.17, -372.27) * mm});
            skLineSegment(sketch, "E205", {"start": v(-104.17, -372.27) * mm, "end": v(-104.17, -336.45) * mm});
            skCircle(sketch, "E206", {"center": v(-182.91, -346.87) * mm, "radius": 2.53 * mm});
            skPoint(sketch, "E207.visualSharp", {"position": v(-218.47, -372.27) * mm});
            skArc(sketch, "E207.filletArc", {"start": v(-218.47, -346.87) * mm, "mid": v(-211.03, -364.84) * mm, "end": v(-193.07, -372.27) * mm});
            skSolve(sketch);
        }
        {
            var Q0;
            Q0=makeQuery(id+"F35.imprint","IMPRINT",FACE,{"disambiguationData":[TD([[makeQuery(id+"F35.imprint","IMPRINT",EDGE,{"derivedFrom":sQuery(id+"F35.wireOp",EDGE,"E190.bottom")}),1.0]])]});
            extrude(context, id + "F36", {"entities" : qUnion([Q0]), "depth" : (getVariable(context, 'T0')) * mm, "offsetDistance" : 25.4 * mm});
        }
        {
            var Q0;
            Q0 = qSketchRegion(id + "F28", true);
            extrude(context, id + "F37", {"entities" : qUnion([Q0]), "depth" : (getVariable(context, 'T0')) * mm, "offsetDistance" : 25.4 * mm});
        }
        {
            var Q0;
            Q0=qCreatedBy(makeId("Top.planeOp"),FACE);
            var sketch = newSketch(context, id + "F38", { "sketchPlane" : qUnion([Q0])});
            skLineSegment(sketch, "E208.bottom", {"start": v(901.06, 294.18) * mm, "end": v(902.1, 294.18) * mm});
            skLineSegment(sketch, "E208.top", {"start": v(901.06, 275.13) * mm, "end": v(916.93, 275.13) * mm});
            skLineSegment(sketch, "E208.left", {"start": v(901.06, 281.48) * mm, "end": v(901.06, 275.13) * mm});
            skLineSegment(sketch, "E208.right", {"start": v(929.63, 278.13) * mm, "end": v(929.63, 275.13) * mm});
            skPoint(sketch, "E208.middle", {"position": v(915.34, 284.65) * mm});
            skLineSegment(sketch, "E209.top", {"start": v(929.63, 269.7) * mm, "end": v(916.93, 269.7) * mm});
            skLineSegment(sketch, "E209.left", {"start": v(929.63, 275.13) * mm, "end": v(929.63, 269.7) * mm});
            skLineSegment(sketch, "E209.right", {"start": v(916.93, 275.13) * mm, "end": v(916.93, 269.7) * mm});
            skLineSegment(sketch, "E210.bottom", {"start": v(901.06, 294.18) * mm, "end": v(895.62, 294.18) * mm});
            skLineSegment(sketch, "E210.top", {"start": v(901.06, 281.48) * mm, "end": v(895.62, 281.48) * mm});
            skLineSegment(sketch, "E210.right", {"start": v(895.62, 294.18) * mm, "end": v(895.62, 281.48) * mm});
            skLineSegment(sketch, "E211", {"start": v(927.98, 280.91) * mm, "end": v(905.15, 293.4) * mm});
            skPoint(sketch, "E212.newPointB", {"position": v(929.63, 294.18) * mm});
            skArc(sketch, "E212.filletArc", {"start": v(905.15, 293.4) * mm, "mid": v(903.68, 293.98) * mm, "end": v(902.1, 294.18) * mm});
            skArc(sketch, "E213.filletArc", {"start": v(929.63, 278.13) * mm, "mid": v(929.19, 279.75) * mm, "end": v(927.98, 280.91) * mm});
            skSolve(sketch);
        }
        {
            var Q0;
            Q0=makeQuery(id+"F38.imprint","IMPRINT",FACE,{"disambiguationData":[TD([[makeQuery(id+"F38.imprint","IMPRINT",EDGE,{"derivedFrom":sQuery(id+"F38.wireOp",EDGE,"E208.bottom")}),-1.0]])]});
            extrude(context, id + "F39", {"entities" : qUnion([Q0]), "depth" : (getVariable(context, 'T0')) * mm, "offsetDistance" : 25.4 * mm});
        }
        {
            var Q0;
            Q0=qCreatedBy(makeId("Top.planeOp"),FACE);
            var sketch = newSketch(context, id + "F40", { "sketchPlane" : qUnion([Q0])});
            skCircle(sketch, "E214", {"center": v(-89.95, 239.51) * mm, "radius": 10.73 * mm});
            skArc(sketch, "E215", {"start": v(-91.85, 241.81) * mm, "mid": v(-89.95, 236.53) * mm, "end": v(-88.05, 241.81) * mm});
            skLineSegment(sketch, "E216", {"start": v(-88.05, 241.81) * mm, "end": v(-91.85, 241.81) * mm});
            skSolve(sketch);
        }
        {
            var Q0;
            Q0=makeQuery(id+"F40.imprint","IMPRINT",FACE,{"disambiguationData":[TD([[makeQuery(id+"F40.imprint","IMPRINT",EDGE,{"derivedFrom":sQuery(id+"F40.wireOp",EDGE,"E214")}),1.0]])]});
            extrude(context, id + "F41", {"entities" : qUnion([Q0]), "depth" : (getVariable(context, 'T0')) * mm, "offsetDistance" : 25.4 * mm});
        }
        {
            var Q0;
            Q0=qCreatedBy(makeId("Top.planeOp"),FACE);
            var sketch = newSketch(context, id + "F42", { "sketchPlane" : qUnion([Q0])});
            skArc(sketch, "E217", {"start": v(-18.45, 117.01) * mm, "mid": v(-43.85, 142.16) * mm, "end": v(-69.25, 117.01) * mm});
            skArc(sketch, "E218", {"start": v(-14.64, 117.01) * mm, "mid": v(-43.85, 145.97) * mm, "end": v(-73.06, 117.01) * mm});
            skLineSegment(sketch, "E219", {"start": v(-43.85, 116.76) * mm, "end": v(-43.85, 40.56) * mm, "construction": true});
            skLineSegment(sketch, "E220", {"start": v(-43.85, 40.56) * mm, "end": v(-75.6, 40.56) * mm, "construction": true});
            skLineSegment(sketch, "E221", {"start": v(-73.06, 117.01) * mm, "end": v(-14.64, 117.01) * mm});
            skLineSegment(sketch, "E222", {"start": v(-75.6, 40.56) * mm, "end": v(-75.6, 116.58) * mm, "construction": true});
            skSolve(sketch);
        }
        {
            var Q0;
            {var subQ0=sQuery(id+"F42.wireOp",EDGE,"E217");Q0=makeQuery(id+"F42.imprint","IMPRINT",FACE,{"disambiguationData":[TD([[makeQuery(id+"F42.imprint","IMPRINT",EDGE,{"derivedFrom":subQ0}),-1.0]])]});}
            var Q1;
            Q1=sQuery(id+"F42.wireOp",EDGE,"E222");
            revolve(context, id + "F43", {"entities" : qUnion([Q0]), "axis" : qUnion([Q1]), "revolveType" : RevolveType.ONE_DIRECTION, "angle" : 86 * degree});
        }
        {
            var Q0;
            Q0=qCreatedBy(makeId("Top.planeOp"),FACE);
            var sketch = newSketch(context, id + "F44", { "sketchPlane" : qUnion([Q0])});
            skArc(sketch, "E223", {"start": v(-71.73, 73.9) * mm, "mid": v(-97.13, 99.05) * mm, "end": v(-122.53, 73.9) * mm});
            skArc(sketch, "E224", {"start": v(-67.92, 73.9) * mm, "mid": v(-97.13, 102.86) * mm, "end": v(-126.34, 73.9) * mm});
            skLineSegment(sketch, "E225", {"start": v(-97.13, 73.65) * mm, "end": v(-97.13, -2.55) * mm, "construction": true});
            skLineSegment(sketch, "E226", {"start": v(-97.13, -2.55) * mm, "end": v(-128.88, -2.55) * mm, "construction": true});
            skLineSegment(sketch, "E227", {"start": v(-126.34, 73.9) * mm, "end": v(-67.92, 73.9) * mm});
            skLineSegment(sketch, "E228", {"start": v(-128.88, -2.55) * mm, "end": v(-128.88, 73.48) * mm, "construction": true});
            skSolve(sketch);
        }
        {
            var Q0;
            {var subQ0=sQuery(id+"F44.wireOp",EDGE,"E223");Q0=makeQuery(id+"F44.imprint","IMPRINT",FACE,{"disambiguationData":[TD([[makeQuery(id+"F44.imprint","IMPRINT",EDGE,{"derivedFrom":subQ0}),-1.0]])]});}
            extrude(context, id + "F45", {"entities" : qUnion([Q0]), "depth" : 152.4 * mm, "offsetDistance" : 25.4 * mm});
        }
        {
            var Q0;
            Q0=qCreatedBy(makeId("Top.planeOp"),FACE);
            var sketch = newSketch(context, id + "F46", { "sketchPlane" : qUnion([Q0])});
            skArc(sketch, "E229", {"start": v(-32.1, 12.15) * mm, "mid": v(-57.5, 37.3) * mm, "end": v(-82.9, 12.15) * mm});
            skArc(sketch, "E230", {"start": v(-28.28, 12.15) * mm, "mid": v(-57.5, 41.1) * mm, "end": v(-86.7, 12.15) * mm});
            skLineSegment(sketch, "E231", {"start": v(-57.5, 11.9) * mm, "end": v(-57.5, -64.3) * mm, "construction": true});
            skLineSegment(sketch, "E232", {"start": v(-57.5, -64.3) * mm, "end": v(-89.24, -64.3) * mm, "construction": true});
            skLineSegment(sketch, "E233", {"start": v(-86.7, 12.15) * mm, "end": v(-28.28, 12.15) * mm});
            skLineSegment(sketch, "E234", {"start": v(-89.24, -64.3) * mm, "end": v(-89.24, 11.72) * mm, "construction": true});
            skSolve(sketch);
        }
        {
            var Q0;
            {var subQ0=sQuery(id+"F46.wireOp",EDGE,"E229");Q0=makeQuery(id+"F46.imprint","IMPRINT",FACE,{"disambiguationData":[TD([[makeQuery(id+"F46.imprint","IMPRINT",EDGE,{"derivedFrom":subQ0}),-1.0]])]});}
            extrude(context, id + "F47", {"entities" : qUnion([Q0]), "depth" : 63.5 * mm, "offsetDistance" : 25.4 * mm});
        }
        {
            var Q0;
            Q0=qCreatedBy(makeId("Top.planeOp"),FACE);
            var sketch = newSketch(context, id + "F48", { "sketchPlane" : qUnion([Q0])});
            skArc(sketch, "E235", {"start": v(7.23, -55.6) * mm, "mid": v(-18.17, -30.45) * mm, "end": v(-43.57, -55.6) * mm});
            skArc(sketch, "E236", {"start": v(11.04, -55.6) * mm, "mid": v(-18.17, -26.64) * mm, "end": v(-47.38, -55.6) * mm});
            skLineSegment(sketch, "E237", {"start": v(-18.17, -55.85) * mm, "end": v(-18.17, -132.05) * mm, "construction": true});
            skLineSegment(sketch, "E238", {"start": v(-18.17, -132.05) * mm, "end": v(-49.92, -132.05) * mm, "construction": true});
            skLineSegment(sketch, "E239", {"start": v(-47.38, -55.6) * mm, "end": v(11.04, -55.6) * mm});
            skLineSegment(sketch, "E240", {"start": v(-49.92, -132.05) * mm, "end": v(-49.92, -56.03) * mm, "construction": true});
            skSolve(sketch);
        }
        {
            var Q0;
            {var subQ0=sQuery(id+"F48.wireOp",EDGE,"E235");Q0=makeQuery(id+"F48.imprint","IMPRINT",FACE,{"disambiguationData":[TD([[makeQuery(id+"F48.imprint","IMPRINT",EDGE,{"derivedFrom":subQ0}),-1.0]])]});}
            extrude(context, id + "F49", {"entities" : qUnion([Q0]), "depth" : 228.6 * mm, "offsetDistance" : 25.4 * mm});
        }
        {
            var Q0;
            Q0=qCreatedBy(makeId("Top.planeOp"),FACE);
            var sketch = newSketch(context, id + "F50", { "sketchPlane" : qUnion([Q0])});
            skCircle(sketch, "E241", {"center": v(128.87, -26.04) * mm, "radius": 16.09 * mm});
            skSolve(sketch);
        }
        {
            var Q0;
            Q0 = qSketchRegion(id + "F50", true);
            extrude(context, id + "F51", {"entities" : qUnion([Q0]), "depth" : 41.27 * mm, "offsetDistance" : 25.4 * mm});
        }
        {
            var Q0;
            Q0=qCreatedBy(makeId("Top.planeOp"),FACE);
            var sketch = newSketch(context, id + "F52", { "sketchPlane" : qUnion([Q0])});
            skLineSegment(sketch, "E242.bottom", {"start": v(70.5, -61.42) * mm, "end": v(45.1, -61.42) * mm});
            skLineSegment(sketch, "E242.left", {"start": v(70.5, -51.44) * mm, "end": v(70.5, -46.54) * mm});
            skLineSegment(sketch, "E242.right", {"start": v(45.1, -51.44) * mm, "end": v(45.1, -46.54) * mm});
            skLineSegment(sketch, "E243", {"start": v(57.8, -24.46) * mm, "end": v(57.8, -61.42) * mm, "construction": true});
            skFitSpline(sketch, "E244", {"points": [v(57.8, -24.46) * mm, v(56.82, -24.58) * mm, v(54.96, -25.22) * mm, v(52.59, -27.25) * mm, v(48.17, -36.92) * mm, v(45.1, -46.54) * mm], "startDerivative": vector(-9.64, -0.68) * mm, "endDerivative": vector(-9.08, -30.67) * mm});
            skPoint(sketch, "E245.orphan", {"position": v(45.1, -24.46) * mm});
            skFitSpline(sketch, "E246.MirrorCS", {"points": [v(57.8, -24.46) * mm, v(58.78, -24.58) * mm, v(60.65, -25.22) * mm, v(63.02, -27.25) * mm, v(67.44, -36.92) * mm, v(70.5, -46.54) * mm], "startDerivative": vector(9.64, -0.68) * mm, "endDerivative": vector(9.08, -30.67) * mm});
            skPoint(sketch, "E247.orphan", {"position": v(70.5, -24.46) * mm});
            skLineSegment(sketch, "E248", {"start": v(45.1, -51.44) * mm, "end": v(70.5, -51.44) * mm});
            skSolve(sketch);
        }
        {
            var Q0;
            Q0 = qSketchRegion(id + "F52", true);
            var Q1;
            Q1=sQuery(id+"F52.wireOp",EDGE,"E242.bottom");
            revolve(context, id + "F53", {"entities" : qUnion([Q0]), "axis" : qUnion([Q1]), "revolveType" : RevolveType.FULL});
        }
        {
            var Q0;
            Q0=qCreatedBy(makeId("Top.planeOp"),FACE);
            var sketch = newSketch(context, id + "F54", { "sketchPlane" : qUnion([Q0])});
            skLineSegment(sketch, "E249.bottom", {"start": v(265.4, 192.62) * mm, "end": v(285.72, 192.62) * mm});
            skLineSegment(sketch, "E249.top", {"start": v(265.4, 111.34) * mm, "end": v(285.72, 111.34) * mm});
            skLineSegment(sketch, "E249.left", {"start": v(262.86, 190.08) * mm, "end": v(262.86, 113.88) * mm});
            skLineSegment(sketch, "E250", {"start": v(285.72, 192.62) * mm, "end": v(285.72, 111.34) * mm, "construction": true});
            skPoint(sketch, "E251.visualSharp", {"position": v(262.86, 192.62) * mm});
            skArc(sketch, "E251.filletArc", {"start": v(265.4, 192.62) * mm, "mid": v(263.6, 191.87) * mm, "end": v(262.86, 190.08) * mm});
            skPoint(sketch, "E252.visualSharp", {"position": v(262.86, 111.34) * mm});
            skArc(sketch, "E252.filletArc", {"start": v(262.86, 113.88) * mm, "mid": v(263.6, 112.08) * mm, "end": v(265.4, 111.34) * mm});
            skArc(sketch, "E253.MirrorCS", {"start": v(308.58, 113.88) * mm, "mid": v(307.84, 112.08) * mm, "end": v(306.04, 111.34) * mm});
            skArc(sketch, "E254.MirrorCS", {"start": v(306.04, 192.62) * mm, "mid": v(307.84, 191.87) * mm, "end": v(308.58, 190.08) * mm});
            skPoint(sketch, "E255.MirrorP", {"position": v(308.58, 192.62) * mm});
            skPoint(sketch, "E256.MirrorP", {"position": v(308.58, 111.34) * mm});
            skLineSegment(sketch, "E257.MirrorCS", {"start": v(308.58, 190.08) * mm, "end": v(308.58, 113.88) * mm});
            skLineSegment(sketch, "E258.MirrorCS", {"start": v(306.04, 192.62) * mm, "end": v(285.72, 192.62) * mm});
            skLineSegment(sketch, "E259.MirrorCS", {"start": v(306.04, 111.34) * mm, "end": v(285.72, 111.34) * mm});
            skSolve(sketch);
        }
        {
            var Q0;
            Q0 = qSketchRegion(id + "F54", true);
            extrude(context, id + "F55", {"entities" : qUnion([Q0]), "depth" : 1.55 * mm, "offsetDistance" : 25.4 * mm});
        }
        {
            var Q0;
            Q0=qCreatedBy(makeId("Top.planeOp"),FACE);
            var sketch = newSketch(context, id + "F56", { "sketchPlane" : qUnion([Q0])});
            skCircle(sketch, "E260", {"center": v(315.34, 0) * mm, "radius": 1.59 * mm});
            skSolve(sketch);
        }
        {
            var Q0;
            Q0 = qSketchRegion(id + "F56", true);
            extrude(context, id + "F57", {"entities" : qUnion([Q0]), "depth" : 63.5 * mm, "offsetDistance" : 25.4 * mm});
        }
        {
            var Q0;
            Q0=makeQuery(id+"F18.opExtrude","CAP_FACE",FACE,{"disambiguationData":[OSD([sQuery(id+"F17.wireOp",EDGE,"E60.bottom"),sQuery(id+"F17.wireOp",EDGE,"E60.top"),sQuery(id+"F17.wireOp",EDGE,"E60.left"),sQuery(id+"F17.wireOp",EDGE,"E60.right"),sQuery(id+"F17.wireOp",EDGE,"E61.filletArc"),sQuery(id+"F17.wireOp",EDGE,"E62.filletArc"),sQuery(id+"F17.wireOp",EDGE,"E63.filletArc"),sQuery(id+"F17.wireOp",EDGE,"E64.filletArc"),sQuery(id+"F17.wireOp",EDGE,"E66.bottom"),sQuery(id+"F17.wireOp",EDGE,"E66.top"),sQuery(id+"F17.wireOp",EDGE,"E66.left"),sQuery(id+"F17.wireOp",EDGE,"E66.right"),sQuery(id+"F17.wireOp",EDGE,"E67.bottom"),sQuery(id+"F17.wireOp",EDGE,"E67.top"),sQuery(id+"F17.wireOp",EDGE,"E67.left"),sQuery(id+"F17.wireOp",EDGE,"E67.right"),sQuery(id+"F17.wireOp",EDGE,"E69.bottom"),sQuery(id+"F17.wireOp",EDGE,"E69.top"),sQuery(id+"F17.wireOp",EDGE,"E69.left"),sQuery(id+"F17.wireOp",EDGE,"E69.right"),sQuery(id+"F17.wireOp",EDGE,"E70.bottom"),sQuery(id+"F17.wireOp",EDGE,"E70.top"),sQuery(id+"F17.wireOp",EDGE,"E70.left"),sQuery(id+"F17.wireOp",EDGE,"E70.right"),sQuery(id+"F17.wireOp",EDGE,"E71"),sQuery(id+"F17.wireOp",EDGE,"E72.1.0"),sQuery(id+"F17.wireOp",EDGE,"E72.1.1"),sQuery(id+"F17.wireOp",EDGE,"E72.1.2"),sQuery(id+"F17.wireOp",EDGE,"E72.1.3"),sQuery(id+"F17.wireOp",EDGE,"E72.1.4"),sQuery(id+"F17.wireOp",EDGE,"E72.1.5"),sQuery(id+"F17.wireOp",EDGE,"E72.1.6"),sQuery(id+"F17.wireOp",EDGE,"E72.1.7"),sQuery(id+"F17.wireOp",EDGE,"E72.1.8"),sQuery(id+"F17.wireOp",EDGE,"E72.1.9"),sQuery(id+"F17.wireOp",EDGE,"E72.1.10"),sQuery(id+"F17.wireOp",EDGE,"E72.1.11"),sQuery(id+"F17.wireOp",EDGE,"E72.1.12"),sQuery(id+"F17.wireOp",EDGE,"E72.1.13"),sQuery(id+"F17.wireOp",EDGE,"E72.1.14"),sQuery(id+"F17.wireOp",EDGE,"E72.1.15"),sQuery(id+"F17.wireOp",EDGE,"E72.1.16"),sQuery(id+"F17.wireOp",EDGE,"E72.2.0"),sQuery(id+"F17.wireOp",EDGE,"E72.2.1"),sQuery(id+"F17.wireOp",EDGE,"E72.2.2"),sQuery(id+"F17.wireOp",EDGE,"E72.2.3"),sQuery(id+"F17.wireOp",EDGE,"E72.2.4"),sQuery(id+"F17.wireOp",EDGE,"E72.2.5"),sQuery(id+"F17.wireOp",EDGE,"E72.2.6"),sQuery(id+"F17.wireOp",EDGE,"E72.2.7"),sQuery(id+"F17.wireOp",EDGE,"E72.2.8"),sQuery(id+"F17.wireOp",EDGE,"E72.2.9"),sQuery(id+"F17.wireOp",EDGE,"E72.2.10"),sQuery(id+"F17.wireOp",EDGE,"E72.2.11"),sQuery(id+"F17.wireOp",EDGE,"E72.2.12"),sQuery(id+"F17.wireOp",EDGE,"E72.2.13"),sQuery(id+"F17.wireOp",EDGE,"E72.2.14"),sQuery(id+"F17.wireOp",EDGE,"E72.2.15"),sQuery(id+"F17.wireOp",EDGE,"E72.2.16"),sQuery(id+"F17.wireOp",EDGE,"E72.3.0"),sQuery(id+"F17.wireOp",EDGE,"E72.3.1"),sQuery(id+"F17.wireOp",EDGE,"E72.3.2"),sQuery(id+"F17.wireOp",EDGE,"E72.3.3"),sQuery(id+"F17.wireOp",EDGE,"E72.3.4"),sQuery(id+"F17.wireOp",EDGE,"E72.3.5"),sQuery(id+"F17.wireOp",EDGE,"E72.3.6"),sQuery(id+"F17.wireOp",EDGE,"E72.3.7"),sQuery(id+"F17.wireOp",EDGE,"E72.3.8"),sQuery(id+"F17.wireOp",EDGE,"E72.3.9"),sQuery(id+"F17.wireOp",EDGE,"E72.3.10"),sQuery(id+"F17.wireOp",EDGE,"E72.3.11"),sQuery(id+"F17.wireOp",EDGE,"E72.3.12"),sQuery(id+"F17.wireOp",EDGE,"E72.3.13"),sQuery(id+"F17.wireOp",EDGE,"E72.3.14"),sQuery(id+"F17.wireOp",EDGE,"E72.3.15"),sQuery(id+"F17.wireOp",EDGE,"E72.3.16"),sQuery(id+"F17.wireOp",EDGE,"E73"),sQuery(id+"F17.wireOp",EDGE,"E74.0.1.0"),sQuery(id+"F17.wireOp",EDGE,"E74.1.0.0"),sQuery(id+"F17.wireOp",EDGE,"E74.1.1.0"),sQuery(id+"F17.wireOp",EDGE,"E75.1.0"),sQuery(id+"F17.wireOp",EDGE,"E75.1.1"),sQuery(id+"F17.wireOp",EDGE,"E75.1.2"),sQuery(id+"F17.wireOp",EDGE,"E75.1.3"),sQuery(id+"F17.wireOp",EDGE,"E76"),sQuery(id+"F17.wireOp",EDGE,"E77"),sQuery(id+"F17.wireOp",EDGE,"E79.MirrorC"),sQuery(id+"F17.wireOp",EDGE,"E78.MirrorC"),sQuery(id+"F17.wireOp",EDGE,"E80.1.0"),sQuery(id+"F17.wireOp",EDGE,"E80.1.1"),sQuery(id+"F17.wireOp",EDGE,"E80.1.2"),sQuery(id+"F17.wireOp",EDGE,"E80.1.3"),sQuery(id+"F17.wireOp",EDGE,"E80.2.0"),sQuery(id+"F17.wireOp",EDGE,"E80.2.1"),sQuery(id+"F17.wireOp",EDGE,"E80.2.2"),sQuery(id+"F17.wireOp",EDGE,"E80.2.3"),sQuery(id+"F17.wireOp",EDGE,"E80.3.0"),sQuery(id+"F17.wireOp",EDGE,"E80.3.1"),sQuery(id+"F17.wireOp",EDGE,"E80.3.2"),sQuery(id+"F17.wireOp",EDGE,"E80.3.3"),sQuery(id+"F17.wireOp",EDGE,"E81.bottom"),sQuery(id+"F17.wireOp",EDGE,"E81.top"),sQuery(id+"F17.wireOp",EDGE,"E81.left"),sQuery(id+"F17.wireOp",EDGE,"E81.right"),sQuery(id+"F17.wireOp",EDGE,"E83.1.0"),sQuery(id+"F17.wireOp",EDGE,"E83.1.1"),sQuery(id+"F17.wireOp",EDGE,"E83.1.2"),sQuery(id+"F17.wireOp",EDGE,"E83.1.3")])],"isStart":false});
            var sketch = newSketch(context, id + "F58", { "sketchPlane" : qUnion([Q0])});
            skLineSegment(sketch, "E261.bottom", {"start": v(82.06, -168.3) * mm, "end": v(84.5, -168.3) * mm});
            skLineSegment(sketch, "E261.top", {"start": v(82.06, -178.45) * mm, "end": v(100.89, -178.45) * mm});
            skLineSegment(sketch, "E261.left", {"start": v(82.06, -168.3) * mm, "end": v(82.06, -178.45) * mm});
            skLineSegment(sketch, "E261.right", {"start": v(100.89, -168.3) * mm, "end": v(100.89, -178.45) * mm});
            skCircle(sketch, "E262", {"center": v(86.34, -175.4) * mm, "radius": 1.52 * mm});
            skCircle(sketch, "E263", {"center": v(95.87, -175.4) * mm, "radius": 1.54 * mm});
            skLineSegment(sketch, "E264", {"start": v(84.5, -168.3) * mm, "end": v(101.4, -162.63) * mm});
            skLineSegment(sketch, "E265", {"start": v(101.73, -163.66) * mm, "end": v(86.5, -168.3) * mm});
            skArc(sketch, "E266", {"start": v(101.73, -163.66) * mm, "mid": v(104.58, -162.18) * mm, "end": v(101.4, -162.63) * mm});
            skLineSegment(sketch, "E267.trimOffspring", {"start": v(86.5, -168.3) * mm, "end": v(100.89, -168.3) * mm});
            skPoint(sketch, "E268.orphan", {"position": v(103.21, -163.21) * mm});
            skPoint(sketch, "E269.start.orphan", {"position": v(102.85, -162.14) * mm});
            skSolve(sketch);
        }
        {
            var Q0;
            Q0 = qSketchRegion(id + "F58", true);
            extrude(context, id + "F59", {"entities" : qUnion([Q0]), "depth" : 7.62 * mm, "offsetDistance" : 25.4 * mm});
        }
        {
            var Q0;
            Q0=qCreatedBy(makeId("Right.planeOp"),FACE);
            var sketch = newSketch(context, id + "F60", { "sketchPlane" : qUnion([Q0])});
            skLineSegment(sketch, "E270.bottom", {"start": v(-443.47, 56.97) * mm, "end": v(-544.92, 56.97) * mm});
            skLineSegment(sketch, "E270.top", {"start": v(-443.47, 73.53) * mm, "end": v(-494.2, 73.53) * mm});
            skLineSegment(sketch, "E270.left", {"start": v(-443.47, 56.97) * mm, "end": v(-443.47, 73.53) * mm});
            skLineSegment(sketch, "E270.right", {"start": v(-544.92, 56.97) * mm, "end": v(-544.92, 73.53) * mm});
            skCircle(sketch, "E271", {"center": v(-522.04, 62.72) * mm, "radius": 4.63 * mm});
            skLineSegment(sketch, "E272.top", {"start": v(-494.2, 68.5) * mm, "end": v(-516.27, 68.5) * mm});
            skLineSegment(sketch, "E272.left", {"start": v(-494.2, 73.53) * mm, "end": v(-494.2, 68.5) * mm});
            skLineSegment(sketch, "E272.right", {"start": v(-516.27, 73.53) * mm, "end": v(-516.27, 68.5) * mm});
            skLineSegment(sketch, "E273.trimOffspring", {"start": v(-516.27, 73.53) * mm, "end": v(-544.92, 73.53) * mm});
            skSolve(sketch);
        }
        {
            var Q0;
            Q0 = qSketchRegion(id + "F60", true);
            extrude(context, id + "F61", {"entities" : qUnion([Q0]), "depth" : (getVariable(context, 'T0')) * mm, "offsetDistance" : 25.4 * mm});
        }
        {
            var Q0;
            Q0=makeQuery(id+"F61.opExtrude","CAP_FACE",FACE,{"disambiguationData":[OSD([sQuery(id+"F60.wireOp",EDGE,"E270.bottom"),sQuery(id+"F60.wireOp",EDGE,"E270.top"),sQuery(id+"F60.wireOp",EDGE,"E270.left"),sQuery(id+"F60.wireOp",EDGE,"E270.right"),sQuery(id+"F60.wireOp",EDGE,"E271"),sQuery(id+"F60.wireOp",EDGE,"E272.top"),sQuery(id+"F60.wireOp",EDGE,"E272.left"),sQuery(id+"F60.wireOp",EDGE,"E272.right"),sQuery(id+"F60.wireOp",EDGE,"E273.trimOffspring")])],"isStart":true});
            var sketch = newSketch(context, id + "F62", { "sketchPlane" : qUnion([Q0])});
            skLineSegment(sketch, "E274", {"start": v(455.38, 59.74) * mm, "end": v(403.07, 52.39) * mm});
            skLineSegment(sketch, "E275", {"start": v(403.07, 52.39) * mm, "end": v(401.14, 66.18) * mm});
            skLineSegment(sketch, "E276", {"start": v(401.14, 66.18) * mm, "end": v(453.44, 73.53) * mm});
            skLineSegment(sketch, "E277", {"start": v(455.38, 59.74) * mm, "end": v(453.44, 73.53) * mm});
            skSolve(sketch);
        }
        {
            var Q0;
            Q0 = qSketchRegion(id + "F62", true);
            extrude(context, id + "F63", {"entities" : qUnion([Q0]), "operationType" : NewBodyOperationType.ADD, "depth" : (getVariable(context, 'T0')) * mm, "offsetDistance" : 25.4 * mm});
        }
        {
            var Q0;
            Q0=makeQuery(id+"F63.opExtrude","SWEPT_FACE",FACE,{"disambiguationData":[OSD([sQuery(id+"F62.wireOp",EDGE,"E274")])]});
            var sketch = newSketch(context, id + "F64", { "sketchPlane" : qUnion([Q0])});
            skLineSegment(sketch, "E278.bottom", {"start": v(-4.96, 465.91) * mm, "end": v(14.1, 465.91) * mm});
            skLineSegment(sketch, "E278.left", {"start": v(-4.96, 465.91) * mm, "end": v(-4.96, 459.56) * mm});
            skLineSegment(sketch, "E278.right", {"start": v(14.1, 465.91) * mm, "end": v(14.1, 459.56) * mm});
            skLineSegment(sketch, "E279.top", {"start": v(0.76, 446.86) * mm, "end": v(8.38, 446.86) * mm});
            skLineSegment(sketch, "E280", {"start": v(4.57, 459.56) * mm, "end": v(4.57, 446.86) * mm, "construction": true});
            skLineSegment(sketch, "E281.MirrorCS", {"start": v(14.1, 459.56) * mm, "end": v(8.38, 446.86) * mm});
            skLineSegment(sketch, "E282.MirrorCS", {"start": v(-4.96, 459.56) * mm, "end": v(0.76, 446.86) * mm});
            skLineSegment(sketch, "E283.trimOffspring", {"start": v(14.1, 459.56) * mm, "end": v(14.1, 459.56) * mm});
            skPoint(sketch, "E284.orphan", {"position": v(9.2, 446.86) * mm});
            skPoint(sketch, "E285.orphan", {"position": v(-0.05, 446.86) * mm});
            skLineSegment(sketch, "E286", {"start": v(-4.96, 459.56) * mm, "end": v(14.1, 459.56) * mm, "construction": true});
            skSolve(sketch);
        }
        {
            var Q0;
            Q0 = qSketchRegion(id + "F64", true);
            extrude(context, id + "F65", {"entities" : qUnion([Q0]), "depth" : 5.08 * mm, "offsetDistance" : 25.4 * mm});
        }
        {
            var Q0;
            Q0=qCreatedBy(makeId("Top.planeOp"),FACE);
            var sketch = newSketch(context, id + "F66", { "sketchPlane" : qUnion([Q0])});
            skCircle(sketch, "E287", {"center": v(36.48, 45.99) * mm, "radius": 6.35 * mm});
            skSolve(sketch);
        }
        {
            var Q0;
            Q0 = qSketchRegion(id + "F66", true);
            extrude(context, id + "F67", {"entities" : qUnion([Q0]), "depth" : 19.05 * mm, "offsetDistance" : 25.4 * mm});
        }
    });
